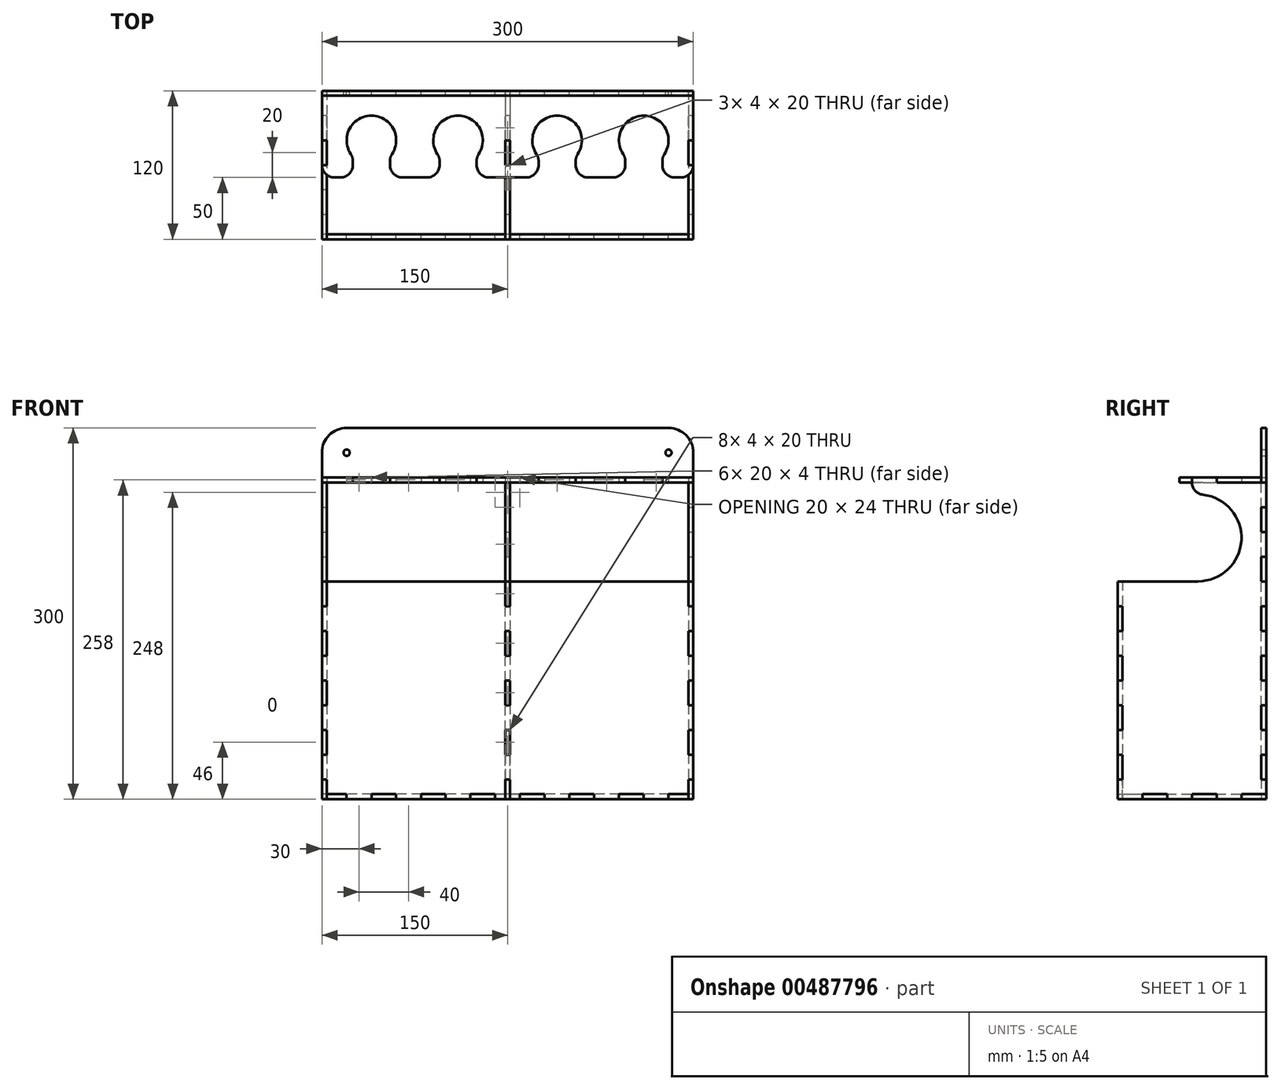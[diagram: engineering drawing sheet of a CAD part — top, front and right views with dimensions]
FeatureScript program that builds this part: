
annotation { "Feature Type Name" : "Feature", "Feature Type Description" : "" }
export const myFeature = defineFeature(function(context is Context, id is Id, definition is map)
    precondition{}
    {
        {
            var Q0;
            Q0=qCreatedBy(makeId("Front.planeOp"),FACE);
            var sketch = newSketch(context, id + "F0", { "sketchPlane" : qUnion([Q0])});
            skLineSegment(sketch, "E0.bottom", {"start": v(-130, 150) * mm, "end": v(130, 150) * mm});
            skLineSegment(sketch, "E0.top", {"start": v(-130, -150) * mm, "end": v(-110, -150) * mm});
            skLineSegment(sketch, "E0.left", {"start": v(-150, 130) * mm, "end": v(-150, 106) * mm});
            skLineSegment(sketch, "E0.right", {"start": v(150, 130) * mm, "end": v(150, 106) * mm});
            skPoint(sketch, "E0.middle", {"position": v(0, 0) * mm});
            skPoint(sketch, "E1.visualSharp", {"position": v(-150, 150) * mm});
            skArc(sketch, "E1.filletArc", {"start": v(-130, 150) * mm, "mid": v(-144.14, 144.14) * mm, "end": v(-150, 130) * mm});
            skPoint(sketch, "E2.visualSharp", {"position": v(150, 150) * mm});
            skArc(sketch, "E2.filletArc", {"start": v(150, 130) * mm, "mid": v(144.14, 144.14) * mm, "end": v(130, 150) * mm});
            skLineSegment(sketch, "E3", {"start": v(-130, 110) * mm, "end": v(-110, 110) * mm});
            skLineSegment(sketch, "E4", {"start": v(-150, 106) * mm, "end": v(-146, 106) * mm});
            skLineSegment(sketch, "E5", {"start": v(-146, 106) * mm, "end": v(-146, 86) * mm});
            skLineSegment(sketch, "E6", {"start": v(146, 106) * mm, "end": v(146, 46) * mm});
            skLineSegment(sketch, "E7", {"start": v(-146, -146) * mm, "end": v(-130, -146) * mm});
            skCircle(sketch, "E8", {"center": v(-130, 130) * mm, "radius": 2.5 * mm});
            skLineSegment(sketch, "E9", {"start": v(-130, 110) * mm, "end": v(-130, 106) * mm});
            skLineSegment(sketch, "E10.1.0.0", {"start": v(-110, 110) * mm, "end": v(-110, 106) * mm});
            skLineSegment(sketch, "E10.2.0.0", {"start": v(-90, 110) * mm, "end": v(-90, 106) * mm});
            skLineSegment(sketch, "E10.3.0.0", {"start": v(-70, 110) * mm, "end": v(-70, 106) * mm});
            skLineSegment(sketch, "E10.4.0.0", {"start": v(-50, 110) * mm, "end": v(-50, 106) * mm});
            skLineSegment(sketch, "E10.5.0.0", {"start": v(-30, 110) * mm, "end": v(-30, 106) * mm});
            skLineSegment(sketch, "E10.6.0.0", {"start": v(-10, 110) * mm, "end": v(-10, 106) * mm});
            skLineSegment(sketch, "E10.7.0.0", {"start": v(10, 110) * mm, "end": v(10, 106) * mm});
            skLineSegment(sketch, "E10.8.0.0", {"start": v(30, 110) * mm, "end": v(30, 106) * mm});
            skLineSegment(sketch, "E10.9.0.0", {"start": v(50, 110) * mm, "end": v(50, 106) * mm});
            skLineSegment(sketch, "E10.10.0.0", {"start": v(70, 110) * mm, "end": v(70, 106) * mm});
            skLineSegment(sketch, "E10.11.0.0", {"start": v(90, 110) * mm, "end": v(90, 106) * mm});
            skLineSegment(sketch, "E10.12.0.0", {"start": v(110, 110) * mm, "end": v(110, 106) * mm});
            skLineSegment(sketch, "E10.13.0.0", {"start": v(130, 110) * mm, "end": v(130, 106) * mm});
            skLineSegment(sketch, "E10.direction1", {"start": v(-130, 106) * mm, "end": v(-110, 106) * mm, "construction": true});
            skLineSegment(sketch, "E11.trimOffspring", {"start": v(-130, 106) * mm, "end": v(-110, 106) * mm});
            skLineSegment(sketch, "E12.trimOffspring", {"start": v(-90, 110) * mm, "end": v(-70, 110) * mm});
            skLineSegment(sketch, "E13.trimOffspring", {"start": v(-90, 106) * mm, "end": v(-70, 106) * mm});
            skLineSegment(sketch, "E14.trimOffspring", {"start": v(-50, 110) * mm, "end": v(-30, 110) * mm});
            skLineSegment(sketch, "E15.trimOffspring", {"start": v(-50, 106) * mm, "end": v(-30, 106) * mm});
            skLineSegment(sketch, "E16.trimOffspring", {"start": v(-10, 110) * mm, "end": v(10, 110) * mm});
            skLineSegment(sketch, "E17.trimOffspring", {"start": v(-10, 106) * mm, "end": v(-2, 106) * mm});
            skLineSegment(sketch, "E18.trimOffspring", {"start": v(30, 110) * mm, "end": v(50, 110) * mm});
            skLineSegment(sketch, "E19.trimOffspring", {"start": v(30, 106) * mm, "end": v(50, 106) * mm});
            skLineSegment(sketch, "E20.trimOffspring", {"start": v(70, 110) * mm, "end": v(90, 110) * mm});
            skLineSegment(sketch, "E21.trimOffspring", {"start": v(70, 106) * mm, "end": v(90, 106) * mm});
            skLineSegment(sketch, "E22.trimOffspring", {"start": v(110, 110) * mm, "end": v(130, 110) * mm});
            skLineSegment(sketch, "E23.trimOffspring", {"start": v(110, 106) * mm, "end": v(130, 106) * mm});
            skLineSegment(sketch, "E24.trimOffspring", {"start": v(146, 106) * mm, "end": v(150, 106) * mm});
            skLineSegment(sketch, "E25", {"start": v(-150, 86) * mm, "end": v(-146, 86) * mm});
            skLineSegment(sketch, "E26.0.1.0", {"start": v(-150, 66) * mm, "end": v(-146, 66) * mm});
            skLineSegment(sketch, "E26.0.2.0", {"start": v(-150, 46) * mm, "end": v(-146, 46) * mm});
            skLineSegment(sketch, "E26.0.3.0", {"start": v(-150, 26) * mm, "end": v(-146, 26) * mm});
            skLineSegment(sketch, "E26.0.4.0", {"start": v(-150, 6) * mm, "end": v(-146, 6) * mm});
            skLineSegment(sketch, "E26.0.5.0", {"start": v(-150, -14) * mm, "end": v(-146, -14) * mm});
            skLineSegment(sketch, "E26.0.6.0", {"start": v(-150, -34) * mm, "end": v(-146, -34) * mm});
            skLineSegment(sketch, "E26.0.7.0", {"start": v(-150, -54) * mm, "end": v(-146, -54) * mm});
            skLineSegment(sketch, "E26.0.8.0", {"start": v(-150, -74) * mm, "end": v(-146, -74) * mm});
            skLineSegment(sketch, "E26.0.9.0", {"start": v(-150, -94) * mm, "end": v(-146, -94) * mm});
            skLineSegment(sketch, "E26.0.10.0", {"start": v(-150, -114) * mm, "end": v(-146, -114) * mm});
            skLineSegment(sketch, "E26.0.11.0", {"start": v(-150, -134) * mm, "end": v(-146, -134) * mm});
            skLineSegment(sketch, "E26.direction1", {"start": v(-150, 86) * mm, "end": v(-125, 86) * mm, "construction": true});
            skLineSegment(sketch, "E26.direction2", {"start": v(-150, 86) * mm, "end": v(-150, 66) * mm, "construction": true});
            skLineSegment(sketch, "E27.trimOffspring", {"start": v(-150, 86) * mm, "end": v(-150, 66) * mm});
            skLineSegment(sketch, "E28.trimOffspring", {"start": v(-146, 66) * mm, "end": v(-146, 46) * mm});
            skLineSegment(sketch, "E29.trimOffspring", {"start": v(-150, 46) * mm, "end": v(-150, 26) * mm});
            skLineSegment(sketch, "E30.trimOffspring", {"start": v(-146, 26) * mm, "end": v(-146, 6) * mm});
            skLineSegment(sketch, "E31.trimOffspring", {"start": v(-150, 6) * mm, "end": v(-150, -14) * mm});
            skLineSegment(sketch, "E32.trimOffspring", {"start": v(-146, -14) * mm, "end": v(-146, -34) * mm});
            skLineSegment(sketch, "E33.trimOffspring", {"start": v(-150, -34) * mm, "end": v(-150, -54) * mm});
            skLineSegment(sketch, "E34.trimOffspring", {"start": v(-146, -54) * mm, "end": v(-146, -74) * mm});
            skLineSegment(sketch, "E35.trimOffspring", {"start": v(-150, -74) * mm, "end": v(-150, -94) * mm});
            skLineSegment(sketch, "E36.trimOffspring", {"start": v(-150, -114) * mm, "end": v(-150, -134) * mm});
            skLineSegment(sketch, "E37.trimOffspring", {"start": v(-146, -134) * mm, "end": v(-146, -146) * mm});
            skLineSegment(sketch, "E38", {"start": v(-130, -146) * mm, "end": v(-130, -150) * mm});
            skLineSegment(sketch, "E39.1.0.0", {"start": v(-110, -146) * mm, "end": v(-110, -150) * mm});
            skLineSegment(sketch, "E39.2.0.0", {"start": v(-90, -146) * mm, "end": v(-90, -150) * mm});
            skLineSegment(sketch, "E39.3.0.0", {"start": v(-70, -146) * mm, "end": v(-70, -150) * mm});
            skLineSegment(sketch, "E39.4.0.0", {"start": v(-50, -146) * mm, "end": v(-50, -150) * mm});
            skLineSegment(sketch, "E39.5.0.0", {"start": v(-30, -146) * mm, "end": v(-30, -150) * mm});
            skLineSegment(sketch, "E39.6.0.0", {"start": v(-10, -146) * mm, "end": v(-10, -150) * mm});
            skLineSegment(sketch, "E39.7.0.0", {"start": v(10, -146) * mm, "end": v(10, -150) * mm});
            skLineSegment(sketch, "E39.8.0.0", {"start": v(30, -146) * mm, "end": v(30, -150) * mm});
            skLineSegment(sketch, "E39.9.0.0", {"start": v(50, -146) * mm, "end": v(50, -150) * mm});
            skLineSegment(sketch, "E39.10.0.0", {"start": v(70, -146) * mm, "end": v(70, -150) * mm});
            skLineSegment(sketch, "E39.11.0.0", {"start": v(90, -146) * mm, "end": v(90, -150) * mm});
            skLineSegment(sketch, "E39.12.0.0", {"start": v(110, -146) * mm, "end": v(110, -150) * mm});
            skLineSegment(sketch, "E39.13.0.0", {"start": v(130, -146) * mm, "end": v(130, -150) * mm});
            skLineSegment(sketch, "E39.direction1", {"start": v(-130, -150) * mm, "end": v(-110, -150) * mm, "construction": true});
            skLineSegment(sketch, "E40.trimOffspring", {"start": v(-110, -146) * mm, "end": v(-90, -146) * mm});
            skLineSegment(sketch, "E41.trimOffspring", {"start": v(-90, -150) * mm, "end": v(-70, -150) * mm});
            skLineSegment(sketch, "E42.trimOffspring", {"start": v(-70, -146) * mm, "end": v(-50, -146) * mm});
            skLineSegment(sketch, "E43.trimOffspring", {"start": v(-50, -150) * mm, "end": v(-30, -150) * mm});
            skLineSegment(sketch, "E44.trimOffspring", {"start": v(-30, -146) * mm, "end": v(-10, -146) * mm});
            skLineSegment(sketch, "E45.trimOffspring", {"start": v(-10, -150) * mm, "end": v(10, -150) * mm});
            skLineSegment(sketch, "E46.trimOffspring", {"start": v(10, -146) * mm, "end": v(30, -146) * mm});
            skLineSegment(sketch, "E47.trimOffspring", {"start": v(30, -150) * mm, "end": v(50, -150) * mm});
            skLineSegment(sketch, "E48.trimOffspring", {"start": v(50, -146) * mm, "end": v(70, -146) * mm});
            skLineSegment(sketch, "E49.trimOffspring", {"start": v(70, -150) * mm, "end": v(90, -150) * mm});
            skLineSegment(sketch, "E50.trimOffspring", {"start": v(90, -146) * mm, "end": v(110, -146) * mm});
            skLineSegment(sketch, "E51.trimOffspring", {"start": v(110, -150) * mm, "end": v(130, -150) * mm});
            skLineSegment(sketch, "E52.trimOffspring", {"start": v(130, -146) * mm, "end": v(146, -146) * mm});
            skLineSegment(sketch, "E53.trimOffspring", {"start": v(-146, -94) * mm, "end": v(-146, -114) * mm});
            skCircle(sketch, "E54.MirrorC", {"center": v(130, 130) * mm, "radius": 2.5 * mm});
            skLineSegment(sketch, "E55", {"start": v(146, 86) * mm, "end": v(150, 86) * mm});
            skLineSegment(sketch, "E56.0.1.0", {"start": v(146, 66) * mm, "end": v(150, 66) * mm});
            skLineSegment(sketch, "E56.0.2.0", {"start": v(146, 46) * mm, "end": v(150, 46) * mm});
            skLineSegment(sketch, "E56.0.3.0", {"start": v(146, 26) * mm, "end": v(150, 26) * mm});
            skLineSegment(sketch, "E56.0.4.0", {"start": v(146, 6) * mm, "end": v(150, 6) * mm});
            skLineSegment(sketch, "E56.0.5.0", {"start": v(146, -14) * mm, "end": v(150, -14) * mm});
            skLineSegment(sketch, "E56.0.6.0", {"start": v(146, -34) * mm, "end": v(150, -34) * mm});
            skLineSegment(sketch, "E56.0.7.0", {"start": v(146, -54) * mm, "end": v(150, -54) * mm});
            skLineSegment(sketch, "E56.0.8.0", {"start": v(146, -74) * mm, "end": v(150, -74) * mm});
            skLineSegment(sketch, "E56.0.9.0", {"start": v(146, -94) * mm, "end": v(150, -94) * mm});
            skLineSegment(sketch, "E56.0.10.0", {"start": v(146, -114) * mm, "end": v(150, -114) * mm});
            skLineSegment(sketch, "E56.0.11.0", {"start": v(146, -134) * mm, "end": v(150, -134) * mm});
            skLineSegment(sketch, "E56.direction1", {"start": v(146, 86) * mm, "end": v(171, 86) * mm, "construction": true});
            skLineSegment(sketch, "E57.trimOffspring", {"start": v(146, -134) * mm, "end": v(146, -146) * mm});
            skLineSegment(sketch, "E58.trimOffspring", {"start": v(150, -114) * mm, "end": v(150, -134) * mm});
            skLineSegment(sketch, "E59.trimOffspring", {"start": v(146, -94) * mm, "end": v(146, -114) * mm});
            skLineSegment(sketch, "E60.trimOffspring", {"start": v(150, -74) * mm, "end": v(150, -94) * mm});
            skLineSegment(sketch, "E61.trimOffspring", {"start": v(146, -54) * mm, "end": v(146, -74) * mm});
            skLineSegment(sketch, "E62.trimOffspring", {"start": v(150, -34) * mm, "end": v(150, -54) * mm});
            skLineSegment(sketch, "E63.trimOffspring", {"start": v(146, -14) * mm, "end": v(146, -34) * mm});
            skLineSegment(sketch, "E64.trimOffspring", {"start": v(150, 6) * mm, "end": v(150, -14) * mm});
            skLineSegment(sketch, "E65.trimOffspring", {"start": v(146, 26) * mm, "end": v(146, 6) * mm});
            skLineSegment(sketch, "E66.trimOffspring", {"start": v(150, 46) * mm, "end": v(150, 26) * mm});
            skLineSegment(sketch, "E67.trimOffspring", {"start": v(150, 86) * mm, "end": v(150, 66) * mm});
            skLineSegment(sketch, "E68.bottom", {"start": v(-2, 86) * mm, "end": v(2, 86) * mm});
            skLineSegment(sketch, "E68.left", {"start": v(-2, 86) * mm, "end": v(-2, 106) * mm});
            skLineSegment(sketch, "E68.right", {"start": v(2, 86) * mm, "end": v(2, 106) * mm});
            skPoint(sketch, "E68.middle", {"position": v(0, 96) * mm});
            skLineSegment(sketch, "E69.0.1.0", {"start": v(-2, 46) * mm, "end": v(-2, 66) * mm});
            skLineSegment(sketch, "E69.0.1.1", {"start": v(2, 46) * mm, "end": v(2, 66) * mm});
            skLineSegment(sketch, "E69.0.1.2", {"start": v(-2, 46) * mm, "end": v(2, 46) * mm});
            skLineSegment(sketch, "E69.0.1.3", {"start": v(-2, 66) * mm, "end": v(2, 66) * mm});
            skPoint(sketch, "E69.0.1.4", {"position": v(0, 56) * mm});
            skLineSegment(sketch, "E69.0.2.0", {"start": v(-2, 6) * mm, "end": v(-2, 26) * mm});
            skLineSegment(sketch, "E69.0.2.1", {"start": v(2, 6) * mm, "end": v(2, 26) * mm});
            skLineSegment(sketch, "E69.0.2.2", {"start": v(-2, 6) * mm, "end": v(2, 6) * mm});
            skLineSegment(sketch, "E69.0.2.3", {"start": v(-2, 26) * mm, "end": v(2, 26) * mm});
            skPoint(sketch, "E69.0.2.4", {"position": v(0, 16) * mm});
            skLineSegment(sketch, "E69.0.3.0", {"start": v(-2, -34) * mm, "end": v(-2, -14) * mm});
            skLineSegment(sketch, "E69.0.3.1", {"start": v(2, -34) * mm, "end": v(2, -14) * mm});
            skLineSegment(sketch, "E69.0.3.2", {"start": v(-2, -34) * mm, "end": v(2, -34) * mm});
            skLineSegment(sketch, "E69.0.3.3", {"start": v(-2, -14) * mm, "end": v(2, -14) * mm});
            skPoint(sketch, "E69.0.3.4", {"position": v(0, -24) * mm});
            skLineSegment(sketch, "E69.0.4.0", {"start": v(-2, -74) * mm, "end": v(-2, -54) * mm});
            skLineSegment(sketch, "E69.0.4.1", {"start": v(2, -74) * mm, "end": v(2, -54) * mm});
            skLineSegment(sketch, "E69.0.4.2", {"start": v(-2, -74) * mm, "end": v(2, -74) * mm});
            skLineSegment(sketch, "E69.0.4.3", {"start": v(-2, -54) * mm, "end": v(2, -54) * mm});
            skPoint(sketch, "E69.0.4.4", {"position": v(0, -64) * mm});
            skLineSegment(sketch, "E69.0.5.0", {"start": v(-2, -114) * mm, "end": v(-2, -94) * mm});
            skLineSegment(sketch, "E69.0.5.1", {"start": v(2, -114) * mm, "end": v(2, -94) * mm});
            skLineSegment(sketch, "E69.0.5.2", {"start": v(-2, -114) * mm, "end": v(2, -114) * mm});
            skLineSegment(sketch, "E69.0.5.3", {"start": v(-2, -94) * mm, "end": v(2, -94) * mm});
            skPoint(sketch, "E69.0.5.4", {"position": v(0, -104) * mm});
            skLineSegment(sketch, "E69.direction1", {"start": v(-2, 86) * mm, "end": v(23, 86) * mm, "construction": true});
            skLineSegment(sketch, "E69.direction2", {"start": v(-2, 86) * mm, "end": v(-2, 46) * mm, "construction": true});
            skLineSegment(sketch, "E70.trimOffspring", {"start": v(2, 106) * mm, "end": v(10, 106) * mm});
            skSolve(sketch);
        }
        {
            var Q0;
            Q0 = qSketchRegion(id + "F0", true);
            extrude(context, id + "F1", {"entities" : qUnion([Q0]), "depth" : 4 * mm});
        }
        {
            var Q0;
            Q0=makeQuery(id+"F1.opExtrude","SWEPT_FACE",FACE,{"disambiguationData":[OSD([sQuery(id+"F0.wireOp",EDGE,"E11.trimOffspring")])]});
            var sketch = newSketch(context, id + "F2", { "sketchPlane" : qUnion([Q0])});
            skLineSegment(sketch, "E71.bottom", {"start": v(-150, 0) * mm, "end": v(150, 0) * mm});
            skLineSegment(sketch, "E71.top", {"start": v(-140, -70) * mm, "end": v(-135, -70) * mm});
            skLineSegment(sketch, "E71.left", {"start": v(-150, 0) * mm, "end": v(-150, -40) * mm});
            skLineSegment(sketch, "E71.right", {"start": v(150, 0) * mm, "end": v(150, -40) * mm});
            skPoint(sketch, "E72.visualSharp", {"position": v(-150, -70) * mm});
            skArc(sketch, "E72.filletArc", {"start": v(-150, -60) * mm, "mid": v(-147.07, -67.07) * mm, "end": v(-140, -70) * mm});
            skPoint(sketch, "E73.visualSharp", {"position": v(150, -70) * mm});
            skArc(sketch, "E73.filletArc", {"start": v(140, -70) * mm, "mid": v(147.07, -67.07) * mm, "end": v(150, -60) * mm});
            skArc(sketch, "E74", {"start": v(-93.33, -51.06) * mm, "mid": v(-110, -20) * mm, "end": v(-126.67, -51.06) * mm});
            skArc(sketch, "E75", {"start": v(-23.33, -51.06) * mm, "mid": v(-40, -20) * mm, "end": v(-56.67, -51.06) * mm});
            skArc(sketch, "E76", {"start": v(56.67, -51.06) * mm, "mid": v(40, -20) * mm, "end": v(23.33, -51.06) * mm});
            skArc(sketch, "E77", {"start": v(126.67, -51.06) * mm, "mid": v(110, -20) * mm, "end": v(93.33, -51.06) * mm});
            skLineSegment(sketch, "E78", {"start": v(-110, -40) * mm, "end": v(-40, -40) * mm, "construction": true});
            skLineSegment(sketch, "E79", {"start": v(40, -40) * mm, "end": v(110, -40) * mm, "construction": true});
            skLineSegment(sketch, "E80", {"start": v(-125, -60) * mm, "end": v(-125, -56.58) * mm});
            skLineSegment(sketch, "E81", {"start": v(-95, -60) * mm, "end": v(-95, -56.58) * mm});
            skLineSegment(sketch, "E82.trimOffspring", {"start": v(-85, -70) * mm, "end": v(-65, -70) * mm});
            skPoint(sketch, "E83.visualSharp", {"position": v(-125, -53.23) * mm});
            skArc(sketch, "E83.filletArc", {"start": v(-125, -56.58) * mm, "mid": v(-125.43, -53.7) * mm, "end": v(-126.67, -51.06) * mm});
            skPoint(sketch, "E84.visualSharp", {"position": v(-125, -70) * mm});
            skArc(sketch, "E84.filletArc", {"start": v(-135, -70) * mm, "mid": v(-127.93, -67.07) * mm, "end": v(-125, -60) * mm});
            skPoint(sketch, "E85.visualSharp", {"position": v(-95, -53.23) * mm});
            skArc(sketch, "E85.filletArc", {"start": v(-93.33, -51.06) * mm, "mid": v(-94.57, -53.7) * mm, "end": v(-95, -56.58) * mm});
            skPoint(sketch, "E86.visualSharp", {"position": v(-95, -70) * mm});
            skArc(sketch, "E86.filletArc", {"start": v(-95, -60) * mm, "mid": v(-92.07, -67.07) * mm, "end": v(-85, -70) * mm});
            skLineSegment(sketch, "E87", {"start": v(-55, -56.58) * mm, "end": v(-55, -60) * mm});
            skLineSegment(sketch, "E88", {"start": v(-25, -56.58) * mm, "end": v(-25, -60) * mm});
            skLineSegment(sketch, "E89.trimOffspring", {"start": v(-15, -70) * mm, "end": v(15, -70) * mm});
            skLineSegment(sketch, "E90", {"start": v(25, -56.58) * mm, "end": v(25, -60) * mm});
            skLineSegment(sketch, "E91", {"start": v(55, -56.58) * mm, "end": v(55, -60) * mm});
            skLineSegment(sketch, "E92", {"start": v(95, -56.58) * mm, "end": v(95, -60) * mm});
            skLineSegment(sketch, "E93", {"start": v(125, -56.58) * mm, "end": v(125, -60) * mm});
            skLineSegment(sketch, "E94.trimOffspring", {"start": v(65, -70) * mm, "end": v(85, -70) * mm});
            skLineSegment(sketch, "E95.trimOffspring", {"start": v(135, -70) * mm, "end": v(140, -70) * mm});
            skPoint(sketch, "E96.visualSharp", {"position": v(-55, -53.23) * mm});
            skArc(sketch, "E96.filletArc", {"start": v(-55, -56.58) * mm, "mid": v(-55.43, -53.7) * mm, "end": v(-56.67, -51.06) * mm});
            skPoint(sketch, "E97.visualSharp", {"position": v(-55, -70) * mm});
            skArc(sketch, "E97.filletArc", {"start": v(-65, -70) * mm, "mid": v(-57.93, -67.07) * mm, "end": v(-55, -60) * mm});
            skPoint(sketch, "E98.visualSharp", {"position": v(-25, -53.23) * mm});
            skArc(sketch, "E98.filletArc", {"start": v(-23.33, -51.06) * mm, "mid": v(-24.57, -53.7) * mm, "end": v(-25, -56.58) * mm});
            skPoint(sketch, "E99.visualSharp", {"position": v(-25, -70) * mm});
            skArc(sketch, "E99.filletArc", {"start": v(-25, -60) * mm, "mid": v(-22.07, -67.07) * mm, "end": v(-15, -70) * mm});
            skPoint(sketch, "E100.visualSharp", {"position": v(25, -53.23) * mm});
            skArc(sketch, "E100.filletArc", {"start": v(25, -56.58) * mm, "mid": v(24.57, -53.7) * mm, "end": v(23.33, -51.06) * mm});
            skPoint(sketch, "E101.visualSharp", {"position": v(25, -70) * mm});
            skArc(sketch, "E101.filletArc", {"start": v(15, -70) * mm, "mid": v(22.07, -67.07) * mm, "end": v(25, -60) * mm});
            skPoint(sketch, "E102.visualSharp", {"position": v(55, -53.23) * mm});
            skArc(sketch, "E102.filletArc", {"start": v(56.67, -51.06) * mm, "mid": v(55.43, -53.7) * mm, "end": v(55, -56.58) * mm});
            skPoint(sketch, "E103.visualSharp", {"position": v(55, -70) * mm});
            skArc(sketch, "E103.filletArc", {"start": v(55, -60) * mm, "mid": v(57.93, -67.07) * mm, "end": v(65, -70) * mm});
            skPoint(sketch, "E104.visualSharp", {"position": v(95, -70) * mm});
            skArc(sketch, "E104.filletArc", {"start": v(85, -70) * mm, "mid": v(92.07, -67.07) * mm, "end": v(95, -60) * mm});
            skPoint(sketch, "E105.visualSharp", {"position": v(95, -53.23) * mm});
            skArc(sketch, "E105.filletArc", {"start": v(95, -56.58) * mm, "mid": v(94.57, -53.7) * mm, "end": v(93.33, -51.06) * mm});
            skPoint(sketch, "E106.visualSharp", {"position": v(125, -53.23) * mm});
            skArc(sketch, "E106.filletArc", {"start": v(126.67, -51.06) * mm, "mid": v(125.43, -53.7) * mm, "end": v(125, -56.58) * mm});
            skPoint(sketch, "E107.visualSharp", {"position": v(125, -70) * mm});
            skArc(sketch, "E107.filletArc", {"start": v(125, -60) * mm, "mid": v(127.93, -67.07) * mm, "end": v(135, -70) * mm});
            skLineSegment(sketch, "E108.bottom", {"start": v(-2, -60) * mm, "end": v(2, -60) * mm});
            skLineSegment(sketch, "E108.top", {"start": v(-2, -40) * mm, "end": v(2, -40) * mm});
            skLineSegment(sketch, "E108.left", {"start": v(-2, -60) * mm, "end": v(-2, -40) * mm});
            skLineSegment(sketch, "E108.right", {"start": v(2, -60) * mm, "end": v(2, -40) * mm});
            skPoint(sketch, "E108.middle", {"position": v(0, -50) * mm});
            skLineSegment(sketch, "E109", {"start": v(-150, -60) * mm, "end": v(-146, -60) * mm});
            skLineSegment(sketch, "E110", {"start": v(-146, -60) * mm, "end": v(-146, -40) * mm});
            skLineSegment(sketch, "E111", {"start": v(-146, -40) * mm, "end": v(-150, -40) * mm});
            skLineSegment(sketch, "E112", {"start": v(150, -60) * mm, "end": v(146, -60) * mm});
            skLineSegment(sketch, "E113", {"start": v(146, -60) * mm, "end": v(146, -40) * mm});
            skLineSegment(sketch, "E114", {"start": v(146, -40) * mm, "end": v(150, -40) * mm});
            skSolve(sketch);
        }
        {
            var Q0;
            Q0 = qSketchRegion(id + "F2", true);
            extrude(context, id + "F3", {"entities" : qUnion([Q0]), "depth" : 4 * mm});
        }
        {
            var Q0;
            Q0=makeQuery(id+"F1.opExtrude","SWEPT_BODY",BODY,{"disambiguationData":[OSD([sQuery(id+"F0.wireOp",EDGE,"E0.bottom"),sQuery(id+"F0.wireOp",EDGE,"E0.top"),sQuery(id+"F0.wireOp",EDGE,"E0.left"),sQuery(id+"F0.wireOp",EDGE,"E0.right"),sQuery(id+"F0.wireOp",EDGE,"E1.filletArc"),sQuery(id+"F0.wireOp",EDGE,"E2.filletArc"),sQuery(id+"F0.wireOp",EDGE,"E3"),sQuery(id+"F0.wireOp",EDGE,"E4"),sQuery(id+"F0.wireOp",EDGE,"E5"),sQuery(id+"F0.wireOp",EDGE,"E6"),sQuery(id+"F0.wireOp",EDGE,"E7"),sQuery(id+"F0.wireOp",EDGE,"E8"),sQuery(id+"F0.wireOp",EDGE,"E9"),sQuery(id+"F0.wireOp",EDGE,"E10.1.0.0"),sQuery(id+"F0.wireOp",EDGE,"E10.2.0.0"),sQuery(id+"F0.wireOp",EDGE,"E10.3.0.0"),sQuery(id+"F0.wireOp",EDGE,"E10.4.0.0"),sQuery(id+"F0.wireOp",EDGE,"E10.5.0.0"),sQuery(id+"F0.wireOp",EDGE,"E10.6.0.0"),sQuery(id+"F0.wireOp",EDGE,"E10.7.0.0"),sQuery(id+"F0.wireOp",EDGE,"E10.8.0.0"),sQuery(id+"F0.wireOp",EDGE,"E10.9.0.0"),sQuery(id+"F0.wireOp",EDGE,"E10.10.0.0"),sQuery(id+"F0.wireOp",EDGE,"E10.11.0.0"),sQuery(id+"F0.wireOp",EDGE,"E10.12.0.0"),sQuery(id+"F0.wireOp",EDGE,"E10.13.0.0"),sQuery(id+"F0.wireOp",EDGE,"E11.trimOffspring"),sQuery(id+"F0.wireOp",EDGE,"E12.trimOffspring"),sQuery(id+"F0.wireOp",EDGE,"E13.trimOffspring"),sQuery(id+"F0.wireOp",EDGE,"E14.trimOffspring"),sQuery(id+"F0.wireOp",EDGE,"E15.trimOffspring"),sQuery(id+"F0.wireOp",EDGE,"E16.trimOffspring"),sQuery(id+"F0.wireOp",EDGE,"E17.trimOffspring"),sQuery(id+"F0.wireOp",EDGE,"E18.trimOffspring"),sQuery(id+"F0.wireOp",EDGE,"E19.trimOffspring"),sQuery(id+"F0.wireOp",EDGE,"E20.trimOffspring"),sQuery(id+"F0.wireOp",EDGE,"E21.trimOffspring"),sQuery(id+"F0.wireOp",EDGE,"E22.trimOffspring"),sQuery(id+"F0.wireOp",EDGE,"E23.trimOffspring"),sQuery(id+"F0.wireOp",EDGE,"E24.trimOffspring"),sQuery(id+"F0.wireOp",EDGE,"E25"),sQuery(id+"F0.wireOp",EDGE,"E26.0.1.0"),sQuery(id+"F0.wireOp",EDGE,"E26.0.2.0"),sQuery(id+"F0.wireOp",EDGE,"E26.0.3.0"),sQuery(id+"F0.wireOp",EDGE,"E26.0.4.0"),sQuery(id+"F0.wireOp",EDGE,"E26.0.5.0"),sQuery(id+"F0.wireOp",EDGE,"E26.0.6.0"),sQuery(id+"F0.wireOp",EDGE,"E26.0.7.0"),sQuery(id+"F0.wireOp",EDGE,"E26.0.8.0"),sQuery(id+"F0.wireOp",EDGE,"E26.0.9.0"),sQuery(id+"F0.wireOp",EDGE,"E26.0.10.0"),sQuery(id+"F0.wireOp",EDGE,"E26.0.11.0"),sQuery(id+"F0.wireOp",EDGE,"E27.trimOffspring"),sQuery(id+"F0.wireOp",EDGE,"E28.trimOffspring"),sQuery(id+"F0.wireOp",EDGE,"E29.trimOffspring"),sQuery(id+"F0.wireOp",EDGE,"E30.trimOffspring"),sQuery(id+"F0.wireOp",EDGE,"E31.trimOffspring"),sQuery(id+"F0.wireOp",EDGE,"E32.trimOffspring"),sQuery(id+"F0.wireOp",EDGE,"E33.trimOffspring"),sQuery(id+"F0.wireOp",EDGE,"E34.trimOffspring"),sQuery(id+"F0.wireOp",EDGE,"E35.trimOffspring"),sQuery(id+"F0.wireOp",EDGE,"E36.trimOffspring"),sQuery(id+"F0.wireOp",EDGE,"E37.trimOffspring"),sQuery(id+"F0.wireOp",EDGE,"E38"),sQuery(id+"F0.wireOp",EDGE,"E39.1.0.0"),sQuery(id+"F0.wireOp",EDGE,"E39.2.0.0"),sQuery(id+"F0.wireOp",EDGE,"E39.3.0.0"),sQuery(id+"F0.wireOp",EDGE,"E39.4.0.0"),sQuery(id+"F0.wireOp",EDGE,"E39.5.0.0"),sQuery(id+"F0.wireOp",EDGE,"E39.6.0.0"),sQuery(id+"F0.wireOp",EDGE,"E39.7.0.0"),sQuery(id+"F0.wireOp",EDGE,"E39.8.0.0"),sQuery(id+"F0.wireOp",EDGE,"E39.9.0.0"),sQuery(id+"F0.wireOp",EDGE,"E39.10.0.0"),sQuery(id+"F0.wireOp",EDGE,"E39.11.0.0"),sQuery(id+"F0.wireOp",EDGE,"E39.12.0.0"),sQuery(id+"F0.wireOp",EDGE,"E39.13.0.0"),sQuery(id+"F0.wireOp",EDGE,"E40.trimOffspring"),sQuery(id+"F0.wireOp",EDGE,"E41.trimOffspring"),sQuery(id+"F0.wireOp",EDGE,"E42.trimOffspring"),sQuery(id+"F0.wireOp",EDGE,"E43.trimOffspring"),sQuery(id+"F0.wireOp",EDGE,"E44.trimOffspring"),sQuery(id+"F0.wireOp",EDGE,"E45.trimOffspring"),sQuery(id+"F0.wireOp",EDGE,"E46.trimOffspring"),sQuery(id+"F0.wireOp",EDGE,"E47.trimOffspring"),sQuery(id+"F0.wireOp",EDGE,"E48.trimOffspring"),sQuery(id+"F0.wireOp",EDGE,"E49.trimOffspring"),sQuery(id+"F0.wireOp",EDGE,"E50.trimOffspring"),sQuery(id+"F0.wireOp",EDGE,"E51.trimOffspring"),sQuery(id+"F0.wireOp",EDGE,"E52.trimOffspring"),sQuery(id+"F0.wireOp",EDGE,"E53.trimOffspring"),sQuery(id+"F0.wireOp",EDGE,"E54.MirrorC"),sQuery(id+"F0.wireOp",EDGE,"E55"),sQuery(id+"F0.wireOp",EDGE,"E56.0.1.0"),sQuery(id+"F0.wireOp",EDGE,"E56.0.2.0"),sQuery(id+"F0.wireOp",EDGE,"E56.0.3.0"),sQuery(id+"F0.wireOp",EDGE,"E56.0.4.0"),sQuery(id+"F0.wireOp",EDGE,"E56.0.5.0"),sQuery(id+"F0.wireOp",EDGE,"E56.0.6.0"),sQuery(id+"F0.wireOp",EDGE,"E56.0.7.0"),sQuery(id+"F0.wireOp",EDGE,"E56.0.8.0"),sQuery(id+"F0.wireOp",EDGE,"E56.0.9.0"),sQuery(id+"F0.wireOp",EDGE,"E56.0.10.0"),sQuery(id+"F0.wireOp",EDGE,"E56.0.11.0"),sQuery(id+"F0.wireOp",EDGE,"E57.trimOffspring"),sQuery(id+"F0.wireOp",EDGE,"E58.trimOffspring"),sQuery(id+"F0.wireOp",EDGE,"E59.trimOffspring"),sQuery(id+"F0.wireOp",EDGE,"E60.trimOffspring"),sQuery(id+"F0.wireOp",EDGE,"E61.trimOffspring"),sQuery(id+"F0.wireOp",EDGE,"E62.trimOffspring"),sQuery(id+"F0.wireOp",EDGE,"E63.trimOffspring"),sQuery(id+"F0.wireOp",EDGE,"E64.trimOffspring"),sQuery(id+"F0.wireOp",EDGE,"E65.trimOffspring"),sQuery(id+"F0.wireOp",EDGE,"E66.trimOffspring"),sQuery(id+"F0.wireOp",EDGE,"E67.trimOffspring"),sQuery(id+"F0.wireOp",EDGE,"E68.bottom"),sQuery(id+"F0.wireOp",EDGE,"E68.left"),sQuery(id+"F0.wireOp",EDGE,"E68.right"),sQuery(id+"F0.wireOp",EDGE,"E69.0.1.0"),sQuery(id+"F0.wireOp",EDGE,"E69.0.1.1"),sQuery(id+"F0.wireOp",EDGE,"E69.0.1.2"),sQuery(id+"F0.wireOp",EDGE,"E69.0.1.3"),sQuery(id+"F0.wireOp",EDGE,"E69.0.2.0"),sQuery(id+"F0.wireOp",EDGE,"E69.0.2.1"),sQuery(id+"F0.wireOp",EDGE,"E69.0.2.2"),sQuery(id+"F0.wireOp",EDGE,"E69.0.2.3"),sQuery(id+"F0.wireOp",EDGE,"E69.0.3.0"),sQuery(id+"F0.wireOp",EDGE,"E69.0.3.1"),sQuery(id+"F0.wireOp",EDGE,"E69.0.3.2"),sQuery(id+"F0.wireOp",EDGE,"E69.0.3.3"),sQuery(id+"F0.wireOp",EDGE,"E69.0.4.0"),sQuery(id+"F0.wireOp",EDGE,"E69.0.4.1"),sQuery(id+"F0.wireOp",EDGE,"E69.0.4.2"),sQuery(id+"F0.wireOp",EDGE,"E69.0.4.3"),sQuery(id+"F0.wireOp",EDGE,"E69.0.5.0"),sQuery(id+"F0.wireOp",EDGE,"E69.0.5.1"),sQuery(id+"F0.wireOp",EDGE,"E69.0.5.2"),sQuery(id+"F0.wireOp",EDGE,"E69.0.5.3"),sQuery(id+"F0.wireOp",EDGE,"E70.trimOffspring")])]});
            var Q1;
            Q1=makeQuery(id+"F3.opExtrude","SWEPT_BODY",BODY,{"disambiguationData":[OSD([sQuery(id+"F2.wireOp",EDGE,"E71.bottom"),sQuery(id+"F2.wireOp",EDGE,"E71.top"),sQuery(id+"F2.wireOp",EDGE,"E71.left"),sQuery(id+"F2.wireOp",EDGE,"E71.right"),sQuery(id+"F2.wireOp",EDGE,"E72.filletArc"),sQuery(id+"F2.wireOp",EDGE,"E73.filletArc"),sQuery(id+"F2.wireOp",EDGE,"E74"),sQuery(id+"F2.wireOp",EDGE,"E75"),sQuery(id+"F2.wireOp",EDGE,"E76"),sQuery(id+"F2.wireOp",EDGE,"E77"),sQuery(id+"F2.wireOp",EDGE,"E80"),sQuery(id+"F2.wireOp",EDGE,"E81"),sQuery(id+"F2.wireOp",EDGE,"E82.trimOffspring"),sQuery(id+"F2.wireOp",EDGE,"E83.filletArc"),sQuery(id+"F2.wireOp",EDGE,"E84.filletArc"),sQuery(id+"F2.wireOp",EDGE,"E85.filletArc"),sQuery(id+"F2.wireOp",EDGE,"E86.filletArc"),sQuery(id+"F2.wireOp",EDGE,"E87"),sQuery(id+"F2.wireOp",EDGE,"E88"),sQuery(id+"F2.wireOp",EDGE,"E89.trimOffspring"),sQuery(id+"F2.wireOp",EDGE,"E90"),sQuery(id+"F2.wireOp",EDGE,"E91"),sQuery(id+"F2.wireOp",EDGE,"E92"),sQuery(id+"F2.wireOp",EDGE,"E93"),sQuery(id+"F2.wireOp",EDGE,"E94.trimOffspring"),sQuery(id+"F2.wireOp",EDGE,"E95.trimOffspring"),sQuery(id+"F2.wireOp",EDGE,"E96.filletArc"),sQuery(id+"F2.wireOp",EDGE,"E97.filletArc"),sQuery(id+"F2.wireOp",EDGE,"E98.filletArc"),sQuery(id+"F2.wireOp",EDGE,"E99.filletArc"),sQuery(id+"F2.wireOp",EDGE,"E100.filletArc"),sQuery(id+"F2.wireOp",EDGE,"E101.filletArc"),sQuery(id+"F2.wireOp",EDGE,"E102.filletArc"),sQuery(id+"F2.wireOp",EDGE,"E103.filletArc"),sQuery(id+"F2.wireOp",EDGE,"E104.filletArc"),sQuery(id+"F2.wireOp",EDGE,"E105.filletArc"),sQuery(id+"F2.wireOp",EDGE,"E106.filletArc"),sQuery(id+"F2.wireOp",EDGE,"E107.filletArc"),sQuery(id+"F2.wireOp",EDGE,"E108.bottom"),sQuery(id+"F2.wireOp",EDGE,"E108.top"),sQuery(id+"F2.wireOp",EDGE,"E108.left"),sQuery(id+"F2.wireOp",EDGE,"E108.right"),sQuery(id+"F2.wireOp",EDGE,"E109"),sQuery(id+"F2.wireOp",EDGE,"E110"),sQuery(id+"F2.wireOp",EDGE,"E111"),sQuery(id+"F2.wireOp",EDGE,"E112"),sQuery(id+"F2.wireOp",EDGE,"E113"),sQuery(id+"F2.wireOp",EDGE,"E114")])]});
            booleanBodies(context, id + "F4", {"operationType" : BooleanOperationType.SUBTRACTION, "tools" : qUnion([Q0]), "targets" : qUnion([Q1]), "keepTools" : true});
        }
        {
            var Q0;
            Q0=makeQuery(id+"F3.opExtrude","SWEPT_FACE",FACE,{"disambiguationData":[OSD([sQuery(id+"F2.wireOp",EDGE,"E71.left")])]});
            var sketch = newSketch(context, id + "F5", { "sketchPlane" : qUnion([Q0])});
            skLineSegment(sketch, "E115", {"start": v(60, 110) * mm, "end": v(0, 110) * mm});
            skLineSegment(sketch, "E116", {"start": v(0, 110) * mm, "end": v(0, -146) * mm});
            skLineSegment(sketch, "E117", {"start": v(20, -150) * mm, "end": v(40, -150) * mm});
            skLineSegment(sketch, "E118", {"start": v(60, 110) * mm, "end": v(60, 106) * mm});
            skLineSegment(sketch, "E119", {"start": v(120, -150) * mm, "end": v(120, -134) * mm});
            skArc(sketch, "E120", {"start": v(51.14, 96.07) * mm, "mid": v(57.46, 99.34) * mm, "end": v(60, 106) * mm});
            skArc(sketch, "E121", {"start": v(51.14, 96.07) * mm, "mid": v(20.06, 59.14) * mm, "end": v(55.15, 26) * mm});
            skLineSegment(sketch, "E122", {"start": v(55.15, 26) * mm, "end": v(120, 26) * mm});
            skLineSegment(sketch, "E123", {"start": v(55.15, 26) * mm, "end": v(0, 26) * mm, "construction": true});
            skLineSegment(sketch, "E124", {"start": v(120, 6) * mm, "end": v(116, 6) * mm});
            skLineSegment(sketch, "E125", {"start": v(116, 6) * mm, "end": v(116, -14) * mm});
            skLineSegment(sketch, "E126", {"start": v(116, -14) * mm, "end": v(120, -14) * mm});
            skLineSegment(sketch, "E127.0.1.0", {"start": v(116, -34) * mm, "end": v(116, -54) * mm});
            skLineSegment(sketch, "E127.0.1.1", {"start": v(116, -54) * mm, "end": v(120, -54) * mm});
            skLineSegment(sketch, "E127.0.1.2", {"start": v(120, -34) * mm, "end": v(116, -34) * mm});
            skLineSegment(sketch, "E127.0.2.0", {"start": v(116, -74) * mm, "end": v(116, -94) * mm});
            skLineSegment(sketch, "E127.0.2.1", {"start": v(116, -94) * mm, "end": v(120, -94) * mm});
            skLineSegment(sketch, "E127.0.2.2", {"start": v(120, -74) * mm, "end": v(116, -74) * mm});
            skLineSegment(sketch, "E127.0.3.0", {"start": v(116, -114) * mm, "end": v(116, -134) * mm});
            skLineSegment(sketch, "E127.0.3.1", {"start": v(116, -134) * mm, "end": v(120, -134) * mm});
            skLineSegment(sketch, "E127.0.3.2", {"start": v(120, -114) * mm, "end": v(116, -114) * mm});
            skLineSegment(sketch, "E127.direction1", {"start": v(116, -14) * mm, "end": v(141, -14) * mm, "construction": true});
            skLineSegment(sketch, "E127.direction2", {"start": v(116, -14) * mm, "end": v(116, -54) * mm, "construction": true});
            skLineSegment(sketch, "E128.trimOffspring", {"start": v(120, -114) * mm, "end": v(120, -94) * mm});
            skLineSegment(sketch, "E129.trimOffspring", {"start": v(120, -74) * mm, "end": v(120, -54) * mm});
            skLineSegment(sketch, "E130.trimOffspring", {"start": v(120, -34) * mm, "end": v(120, -14) * mm});
            skLineSegment(sketch, "E131.trimOffspring", {"start": v(120, 6) * mm, "end": v(120, 26) * mm});
            skLineSegment(sketch, "E132", {"start": v(0, -146) * mm, "end": v(20, -146) * mm});
            skLineSegment(sketch, "E133", {"start": v(20, -146) * mm, "end": v(20, -150) * mm});
            skLineSegment(sketch, "E134.1.0.0", {"start": v(40, -146) * mm, "end": v(40, -150) * mm});
            skLineSegment(sketch, "E134.2.0.0", {"start": v(60, -146) * mm, "end": v(60, -150) * mm});
            skLineSegment(sketch, "E134.3.0.0", {"start": v(80, -146) * mm, "end": v(80, -150) * mm});
            skLineSegment(sketch, "E134.4.0.0", {"start": v(100, -146) * mm, "end": v(100, -150) * mm});
            skLineSegment(sketch, "E134.direction1", {"start": v(20, -150) * mm, "end": v(40, -150) * mm, "construction": true});
            skLineSegment(sketch, "E135", {"start": v(40, -146) * mm, "end": v(60, -146) * mm});
            skLineSegment(sketch, "E136", {"start": v(80, -146) * mm, "end": v(100, -146) * mm});
            skLineSegment(sketch, "E137.trimOffspring", {"start": v(60, -150) * mm, "end": v(80, -150) * mm});
            skLineSegment(sketch, "E138.trimOffspring", {"start": v(100, -150) * mm, "end": v(120, -150) * mm});
            skSolve(sketch);
        }
        {
            var Q0;
            {var subQ0=sQuery(id+"F5.wireOp",EDGE,"E116");Q0=makeQuery(id+"F5.imprint","IMPRINT",FACE,{"disambiguationData":[TD([[makeQuery(id+"F5.imprint","IMPRINT",EDGE,{"derivedFrom":subQ0}),1.0]])]});}
            extrude(context, id + "F6", {"entities" : qUnion([Q0]), "oppositeDirection" : true, "depth" : 4 * mm});
        }
        {
            var Q0;
            Q0=makeQuery(id+"F6.opExtrude","SWEPT_BODY",BODY,{"disambiguationData":[OSD([sQuery(id+"F0.wireOp",EDGE,"E0.left"),sQuery(id+"F2.wireOp",EDGE,"E71.left"),sQuery(id+"F2.wireOp",EDGE,"E111"),sQuery(id+"F5.wireOp",EDGE,"E115"),sQuery(id+"F5.wireOp",EDGE,"E116"),sQuery(id+"F5.wireOp",EDGE,"E117"),sQuery(id+"F5.wireOp",EDGE,"E118"),sQuery(id+"F5.wireOp",EDGE,"E119"),sQuery(id+"F5.wireOp",EDGE,"E120"),sQuery(id+"F5.wireOp",EDGE,"E121"),sQuery(id+"F5.wireOp",EDGE,"E122"),sQuery(id+"F5.wireOp",EDGE,"E124"),sQuery(id+"F5.wireOp",EDGE,"E125"),sQuery(id+"F5.wireOp",EDGE,"E126"),sQuery(id+"F5.wireOp",EDGE,"E127.0.1.0"),sQuery(id+"F5.wireOp",EDGE,"E127.0.1.1"),sQuery(id+"F5.wireOp",EDGE,"E127.0.1.2"),sQuery(id+"F5.wireOp",EDGE,"E127.0.2.0"),sQuery(id+"F5.wireOp",EDGE,"E127.0.2.1"),sQuery(id+"F5.wireOp",EDGE,"E127.0.2.2"),sQuery(id+"F5.wireOp",EDGE,"E127.0.3.0"),sQuery(id+"F5.wireOp",EDGE,"E127.0.3.1"),sQuery(id+"F5.wireOp",EDGE,"E127.0.3.2"),sQuery(id+"F5.wireOp",EDGE,"E128.trimOffspring"),sQuery(id+"F5.wireOp",EDGE,"E129.trimOffspring"),sQuery(id+"F5.wireOp",EDGE,"E130.trimOffspring"),sQuery(id+"F5.wireOp",EDGE,"E131.trimOffspring"),sQuery(id+"F5.wireOp",EDGE,"E132"),sQuery(id+"F5.wireOp",EDGE,"E133"),sQuery(id+"F5.wireOp",EDGE,"E134.1.0.0"),sQuery(id+"F5.wireOp",EDGE,"E134.2.0.0"),sQuery(id+"F5.wireOp",EDGE,"E134.3.0.0"),sQuery(id+"F5.wireOp",EDGE,"E134.4.0.0"),sQuery(id+"F5.wireOp",EDGE,"E135"),sQuery(id+"F5.wireOp",EDGE,"E136"),sQuery(id+"F5.wireOp",EDGE,"E137.trimOffspring"),sQuery(id+"F5.wireOp",EDGE,"E138.trimOffspring")])]});
            transform(context, id + "F7", {"entities" : qUnion([Q0]), "transformType" : TransformType.TRANSLATION_3D, "dx" : 148 * mm, "dy" : 0 * mm, "dz" : 0 * mm, "makeCopy" : true});
        }
        {
            var Q0;
            Q0=makeQuery(id+"F1.opExtrude","SWEPT_BODY",BODY,{"disambiguationData":[OSD([sQuery(id+"F0.wireOp",EDGE,"E0.bottom"),sQuery(id+"F0.wireOp",EDGE,"E0.top"),sQuery(id+"F0.wireOp",EDGE,"E0.left"),sQuery(id+"F0.wireOp",EDGE,"E0.right"),sQuery(id+"F0.wireOp",EDGE,"E1.filletArc"),sQuery(id+"F0.wireOp",EDGE,"E2.filletArc"),sQuery(id+"F0.wireOp",EDGE,"E3"),sQuery(id+"F0.wireOp",EDGE,"E4"),sQuery(id+"F0.wireOp",EDGE,"E5"),sQuery(id+"F0.wireOp",EDGE,"E6"),sQuery(id+"F0.wireOp",EDGE,"E7"),sQuery(id+"F0.wireOp",EDGE,"E8"),sQuery(id+"F0.wireOp",EDGE,"E9"),sQuery(id+"F0.wireOp",EDGE,"E10.1.0.0"),sQuery(id+"F0.wireOp",EDGE,"E10.2.0.0"),sQuery(id+"F0.wireOp",EDGE,"E10.3.0.0"),sQuery(id+"F0.wireOp",EDGE,"E10.4.0.0"),sQuery(id+"F0.wireOp",EDGE,"E10.5.0.0"),sQuery(id+"F0.wireOp",EDGE,"E10.6.0.0"),sQuery(id+"F0.wireOp",EDGE,"E10.7.0.0"),sQuery(id+"F0.wireOp",EDGE,"E10.8.0.0"),sQuery(id+"F0.wireOp",EDGE,"E10.9.0.0"),sQuery(id+"F0.wireOp",EDGE,"E10.10.0.0"),sQuery(id+"F0.wireOp",EDGE,"E10.11.0.0"),sQuery(id+"F0.wireOp",EDGE,"E10.12.0.0"),sQuery(id+"F0.wireOp",EDGE,"E10.13.0.0"),sQuery(id+"F0.wireOp",EDGE,"E11.trimOffspring"),sQuery(id+"F0.wireOp",EDGE,"E12.trimOffspring"),sQuery(id+"F0.wireOp",EDGE,"E13.trimOffspring"),sQuery(id+"F0.wireOp",EDGE,"E14.trimOffspring"),sQuery(id+"F0.wireOp",EDGE,"E15.trimOffspring"),sQuery(id+"F0.wireOp",EDGE,"E16.trimOffspring"),sQuery(id+"F0.wireOp",EDGE,"E17.trimOffspring"),sQuery(id+"F0.wireOp",EDGE,"E18.trimOffspring"),sQuery(id+"F0.wireOp",EDGE,"E19.trimOffspring"),sQuery(id+"F0.wireOp",EDGE,"E20.trimOffspring"),sQuery(id+"F0.wireOp",EDGE,"E21.trimOffspring"),sQuery(id+"F0.wireOp",EDGE,"E22.trimOffspring"),sQuery(id+"F0.wireOp",EDGE,"E23.trimOffspring"),sQuery(id+"F0.wireOp",EDGE,"E24.trimOffspring"),sQuery(id+"F0.wireOp",EDGE,"E25"),sQuery(id+"F0.wireOp",EDGE,"E26.0.1.0"),sQuery(id+"F0.wireOp",EDGE,"E26.0.2.0"),sQuery(id+"F0.wireOp",EDGE,"E26.0.3.0"),sQuery(id+"F0.wireOp",EDGE,"E26.0.4.0"),sQuery(id+"F0.wireOp",EDGE,"E26.0.5.0"),sQuery(id+"F0.wireOp",EDGE,"E26.0.6.0"),sQuery(id+"F0.wireOp",EDGE,"E26.0.7.0"),sQuery(id+"F0.wireOp",EDGE,"E26.0.8.0"),sQuery(id+"F0.wireOp",EDGE,"E26.0.9.0"),sQuery(id+"F0.wireOp",EDGE,"E26.0.10.0"),sQuery(id+"F0.wireOp",EDGE,"E26.0.11.0"),sQuery(id+"F0.wireOp",EDGE,"E27.trimOffspring"),sQuery(id+"F0.wireOp",EDGE,"E28.trimOffspring"),sQuery(id+"F0.wireOp",EDGE,"E29.trimOffspring"),sQuery(id+"F0.wireOp",EDGE,"E30.trimOffspring"),sQuery(id+"F0.wireOp",EDGE,"E31.trimOffspring"),sQuery(id+"F0.wireOp",EDGE,"E32.trimOffspring"),sQuery(id+"F0.wireOp",EDGE,"E33.trimOffspring"),sQuery(id+"F0.wireOp",EDGE,"E34.trimOffspring"),sQuery(id+"F0.wireOp",EDGE,"E35.trimOffspring"),sQuery(id+"F0.wireOp",EDGE,"E36.trimOffspring"),sQuery(id+"F0.wireOp",EDGE,"E37.trimOffspring"),sQuery(id+"F0.wireOp",EDGE,"E38"),sQuery(id+"F0.wireOp",EDGE,"E39.1.0.0"),sQuery(id+"F0.wireOp",EDGE,"E39.2.0.0"),sQuery(id+"F0.wireOp",EDGE,"E39.3.0.0"),sQuery(id+"F0.wireOp",EDGE,"E39.4.0.0"),sQuery(id+"F0.wireOp",EDGE,"E39.5.0.0"),sQuery(id+"F0.wireOp",EDGE,"E39.6.0.0"),sQuery(id+"F0.wireOp",EDGE,"E39.7.0.0"),sQuery(id+"F0.wireOp",EDGE,"E39.8.0.0"),sQuery(id+"F0.wireOp",EDGE,"E39.9.0.0"),sQuery(id+"F0.wireOp",EDGE,"E39.10.0.0"),sQuery(id+"F0.wireOp",EDGE,"E39.11.0.0"),sQuery(id+"F0.wireOp",EDGE,"E39.12.0.0"),sQuery(id+"F0.wireOp",EDGE,"E39.13.0.0"),sQuery(id+"F0.wireOp",EDGE,"E40.trimOffspring"),sQuery(id+"F0.wireOp",EDGE,"E41.trimOffspring"),sQuery(id+"F0.wireOp",EDGE,"E42.trimOffspring"),sQuery(id+"F0.wireOp",EDGE,"E43.trimOffspring"),sQuery(id+"F0.wireOp",EDGE,"E44.trimOffspring"),sQuery(id+"F0.wireOp",EDGE,"E45.trimOffspring"),sQuery(id+"F0.wireOp",EDGE,"E46.trimOffspring"),sQuery(id+"F0.wireOp",EDGE,"E47.trimOffspring"),sQuery(id+"F0.wireOp",EDGE,"E48.trimOffspring"),sQuery(id+"F0.wireOp",EDGE,"E49.trimOffspring"),sQuery(id+"F0.wireOp",EDGE,"E50.trimOffspring"),sQuery(id+"F0.wireOp",EDGE,"E51.trimOffspring"),sQuery(id+"F0.wireOp",EDGE,"E52.trimOffspring"),sQuery(id+"F0.wireOp",EDGE,"E53.trimOffspring"),sQuery(id+"F0.wireOp",EDGE,"E54.MirrorC"),sQuery(id+"F0.wireOp",EDGE,"E55"),sQuery(id+"F0.wireOp",EDGE,"E56.0.1.0"),sQuery(id+"F0.wireOp",EDGE,"E56.0.2.0"),sQuery(id+"F0.wireOp",EDGE,"E56.0.3.0"),sQuery(id+"F0.wireOp",EDGE,"E56.0.4.0"),sQuery(id+"F0.wireOp",EDGE,"E56.0.5.0"),sQuery(id+"F0.wireOp",EDGE,"E56.0.6.0"),sQuery(id+"F0.wireOp",EDGE,"E56.0.7.0"),sQuery(id+"F0.wireOp",EDGE,"E56.0.8.0"),sQuery(id+"F0.wireOp",EDGE,"E56.0.9.0"),sQuery(id+"F0.wireOp",EDGE,"E56.0.10.0"),sQuery(id+"F0.wireOp",EDGE,"E56.0.11.0"),sQuery(id+"F0.wireOp",EDGE,"E57.trimOffspring"),sQuery(id+"F0.wireOp",EDGE,"E58.trimOffspring"),sQuery(id+"F0.wireOp",EDGE,"E59.trimOffspring"),sQuery(id+"F0.wireOp",EDGE,"E60.trimOffspring"),sQuery(id+"F0.wireOp",EDGE,"E61.trimOffspring"),sQuery(id+"F0.wireOp",EDGE,"E62.trimOffspring"),sQuery(id+"F0.wireOp",EDGE,"E63.trimOffspring"),sQuery(id+"F0.wireOp",EDGE,"E64.trimOffspring"),sQuery(id+"F0.wireOp",EDGE,"E65.trimOffspring"),sQuery(id+"F0.wireOp",EDGE,"E66.trimOffspring"),sQuery(id+"F0.wireOp",EDGE,"E67.trimOffspring"),sQuery(id+"F0.wireOp",EDGE,"E68.bottom"),sQuery(id+"F0.wireOp",EDGE,"E68.left"),sQuery(id+"F0.wireOp",EDGE,"E68.right"),sQuery(id+"F0.wireOp",EDGE,"E69.0.1.0"),sQuery(id+"F0.wireOp",EDGE,"E69.0.1.1"),sQuery(id+"F0.wireOp",EDGE,"E69.0.1.2"),sQuery(id+"F0.wireOp",EDGE,"E69.0.1.3"),sQuery(id+"F0.wireOp",EDGE,"E69.0.2.0"),sQuery(id+"F0.wireOp",EDGE,"E69.0.2.1"),sQuery(id+"F0.wireOp",EDGE,"E69.0.2.2"),sQuery(id+"F0.wireOp",EDGE,"E69.0.2.3"),sQuery(id+"F0.wireOp",EDGE,"E69.0.3.0"),sQuery(id+"F0.wireOp",EDGE,"E69.0.3.1"),sQuery(id+"F0.wireOp",EDGE,"E69.0.3.2"),sQuery(id+"F0.wireOp",EDGE,"E69.0.3.3"),sQuery(id+"F0.wireOp",EDGE,"E69.0.4.0"),sQuery(id+"F0.wireOp",EDGE,"E69.0.4.1"),sQuery(id+"F0.wireOp",EDGE,"E69.0.4.2"),sQuery(id+"F0.wireOp",EDGE,"E69.0.4.3"),sQuery(id+"F0.wireOp",EDGE,"E69.0.5.0"),sQuery(id+"F0.wireOp",EDGE,"E69.0.5.1"),sQuery(id+"F0.wireOp",EDGE,"E69.0.5.2"),sQuery(id+"F0.wireOp",EDGE,"E69.0.5.3"),sQuery(id+"F0.wireOp",EDGE,"E70.trimOffspring")])]});
            var Q1;
            Q1=makeQuery(id+"F3.opExtrude","SWEPT_BODY",BODY,{"disambiguationData":[OSD([sQuery(id+"F2.wireOp",EDGE,"E71.bottom"),sQuery(id+"F2.wireOp",EDGE,"E71.top"),sQuery(id+"F2.wireOp",EDGE,"E71.left"),sQuery(id+"F2.wireOp",EDGE,"E71.right"),sQuery(id+"F2.wireOp",EDGE,"E72.filletArc"),sQuery(id+"F2.wireOp",EDGE,"E73.filletArc"),sQuery(id+"F2.wireOp",EDGE,"E74"),sQuery(id+"F2.wireOp",EDGE,"E75"),sQuery(id+"F2.wireOp",EDGE,"E76"),sQuery(id+"F2.wireOp",EDGE,"E77"),sQuery(id+"F2.wireOp",EDGE,"E80"),sQuery(id+"F2.wireOp",EDGE,"E81"),sQuery(id+"F2.wireOp",EDGE,"E82.trimOffspring"),sQuery(id+"F2.wireOp",EDGE,"E83.filletArc"),sQuery(id+"F2.wireOp",EDGE,"E84.filletArc"),sQuery(id+"F2.wireOp",EDGE,"E85.filletArc"),sQuery(id+"F2.wireOp",EDGE,"E86.filletArc"),sQuery(id+"F2.wireOp",EDGE,"E87"),sQuery(id+"F2.wireOp",EDGE,"E88"),sQuery(id+"F2.wireOp",EDGE,"E89.trimOffspring"),sQuery(id+"F2.wireOp",EDGE,"E90"),sQuery(id+"F2.wireOp",EDGE,"E91"),sQuery(id+"F2.wireOp",EDGE,"E92"),sQuery(id+"F2.wireOp",EDGE,"E93"),sQuery(id+"F2.wireOp",EDGE,"E94.trimOffspring"),sQuery(id+"F2.wireOp",EDGE,"E95.trimOffspring"),sQuery(id+"F2.wireOp",EDGE,"E96.filletArc"),sQuery(id+"F2.wireOp",EDGE,"E97.filletArc"),sQuery(id+"F2.wireOp",EDGE,"E98.filletArc"),sQuery(id+"F2.wireOp",EDGE,"E99.filletArc"),sQuery(id+"F2.wireOp",EDGE,"E100.filletArc"),sQuery(id+"F2.wireOp",EDGE,"E101.filletArc"),sQuery(id+"F2.wireOp",EDGE,"E102.filletArc"),sQuery(id+"F2.wireOp",EDGE,"E103.filletArc"),sQuery(id+"F2.wireOp",EDGE,"E104.filletArc"),sQuery(id+"F2.wireOp",EDGE,"E105.filletArc"),sQuery(id+"F2.wireOp",EDGE,"E106.filletArc"),sQuery(id+"F2.wireOp",EDGE,"E107.filletArc"),sQuery(id+"F2.wireOp",EDGE,"E108.bottom"),sQuery(id+"F2.wireOp",EDGE,"E108.top"),sQuery(id+"F2.wireOp",EDGE,"E108.left"),sQuery(id+"F2.wireOp",EDGE,"E108.right"),sQuery(id+"F2.wireOp",EDGE,"E109"),sQuery(id+"F2.wireOp",EDGE,"E110"),sQuery(id+"F2.wireOp",EDGE,"E111"),sQuery(id+"F2.wireOp",EDGE,"E112"),sQuery(id+"F2.wireOp",EDGE,"E113"),sQuery(id+"F2.wireOp",EDGE,"E114")])]});
            var Q2;
            Q2=makeQuery(id+"F6.opExtrude","SWEPT_BODY",BODY,{"disambiguationData":[OSD([sQuery(id+"F0.wireOp",EDGE,"E0.left"),sQuery(id+"F2.wireOp",EDGE,"E71.left"),sQuery(id+"F2.wireOp",EDGE,"E111"),sQuery(id+"F5.wireOp",EDGE,"E115"),sQuery(id+"F5.wireOp",EDGE,"E116"),sQuery(id+"F5.wireOp",EDGE,"E117"),sQuery(id+"F5.wireOp",EDGE,"E118"),sQuery(id+"F5.wireOp",EDGE,"E119"),sQuery(id+"F5.wireOp",EDGE,"E120"),sQuery(id+"F5.wireOp",EDGE,"E121"),sQuery(id+"F5.wireOp",EDGE,"E122"),sQuery(id+"F5.wireOp",EDGE,"E124"),sQuery(id+"F5.wireOp",EDGE,"E125"),sQuery(id+"F5.wireOp",EDGE,"E126"),sQuery(id+"F5.wireOp",EDGE,"E127.0.1.0"),sQuery(id+"F5.wireOp",EDGE,"E127.0.1.1"),sQuery(id+"F5.wireOp",EDGE,"E127.0.1.2"),sQuery(id+"F5.wireOp",EDGE,"E127.0.2.0"),sQuery(id+"F5.wireOp",EDGE,"E127.0.2.1"),sQuery(id+"F5.wireOp",EDGE,"E127.0.2.2"),sQuery(id+"F5.wireOp",EDGE,"E127.0.3.0"),sQuery(id+"F5.wireOp",EDGE,"E127.0.3.1"),sQuery(id+"F5.wireOp",EDGE,"E127.0.3.2"),sQuery(id+"F5.wireOp",EDGE,"E128.trimOffspring"),sQuery(id+"F5.wireOp",EDGE,"E129.trimOffspring"),sQuery(id+"F5.wireOp",EDGE,"E130.trimOffspring"),sQuery(id+"F5.wireOp",EDGE,"E131.trimOffspring"),sQuery(id+"F5.wireOp",EDGE,"E132"),sQuery(id+"F5.wireOp",EDGE,"E133"),sQuery(id+"F5.wireOp",EDGE,"E134.1.0.0"),sQuery(id+"F5.wireOp",EDGE,"E134.2.0.0"),sQuery(id+"F5.wireOp",EDGE,"E134.3.0.0"),sQuery(id+"F5.wireOp",EDGE,"E134.4.0.0"),sQuery(id+"F5.wireOp",EDGE,"E135"),sQuery(id+"F5.wireOp",EDGE,"E136"),sQuery(id+"F5.wireOp",EDGE,"E137.trimOffspring"),sQuery(id+"F5.wireOp",EDGE,"E138.trimOffspring")])]});
            booleanBodies(context, id + "F8", {"operationType" : BooleanOperationType.SUBTRACTION, "tools" : qUnion([Q0, Q1]), "targets" : qUnion([Q2]), "keepTools" : true});
        }
        {
            var Q0;
            Q0=makeQuery(id+"F6.opExtrude","SWEPT_BODY",BODY,{"disambiguationData":[OSD([sQuery(id+"F0.wireOp",EDGE,"E0.left"),sQuery(id+"F2.wireOp",EDGE,"E71.left"),sQuery(id+"F2.wireOp",EDGE,"E111"),sQuery(id+"F5.wireOp",EDGE,"E115"),sQuery(id+"F5.wireOp",EDGE,"E116"),sQuery(id+"F5.wireOp",EDGE,"E117"),sQuery(id+"F5.wireOp",EDGE,"E118"),sQuery(id+"F5.wireOp",EDGE,"E119"),sQuery(id+"F5.wireOp",EDGE,"E120"),sQuery(id+"F5.wireOp",EDGE,"E121"),sQuery(id+"F5.wireOp",EDGE,"E122"),sQuery(id+"F5.wireOp",EDGE,"E124"),sQuery(id+"F5.wireOp",EDGE,"E125"),sQuery(id+"F5.wireOp",EDGE,"E126"),sQuery(id+"F5.wireOp",EDGE,"E127.0.1.0"),sQuery(id+"F5.wireOp",EDGE,"E127.0.1.1"),sQuery(id+"F5.wireOp",EDGE,"E127.0.1.2"),sQuery(id+"F5.wireOp",EDGE,"E127.0.2.0"),sQuery(id+"F5.wireOp",EDGE,"E127.0.2.1"),sQuery(id+"F5.wireOp",EDGE,"E127.0.2.2"),sQuery(id+"F5.wireOp",EDGE,"E127.0.3.0"),sQuery(id+"F5.wireOp",EDGE,"E127.0.3.1"),sQuery(id+"F5.wireOp",EDGE,"E127.0.3.2"),sQuery(id+"F5.wireOp",EDGE,"E128.trimOffspring"),sQuery(id+"F5.wireOp",EDGE,"E129.trimOffspring"),sQuery(id+"F5.wireOp",EDGE,"E130.trimOffspring"),sQuery(id+"F5.wireOp",EDGE,"E131.trimOffspring"),sQuery(id+"F5.wireOp",EDGE,"E132"),sQuery(id+"F5.wireOp",EDGE,"E133"),sQuery(id+"F5.wireOp",EDGE,"E134.1.0.0"),sQuery(id+"F5.wireOp",EDGE,"E134.2.0.0"),sQuery(id+"F5.wireOp",EDGE,"E134.3.0.0"),sQuery(id+"F5.wireOp",EDGE,"E134.4.0.0"),sQuery(id+"F5.wireOp",EDGE,"E135"),sQuery(id+"F5.wireOp",EDGE,"E136"),sQuery(id+"F5.wireOp",EDGE,"E137.trimOffspring"),sQuery(id+"F5.wireOp",EDGE,"E138.trimOffspring")])]});
            transform(context, id + "F9", {"entities" : qUnion([Q0]), "transformType" : TransformType.TRANSLATION_3D, "dx" : 296 * mm, "dy" : 0 * mm, "dz" : 0 * mm, "makeCopy" : true});
        }
        {
            var Q0;
            Q0=makeQuery(id+"F1.opExtrude","SWEPT_BODY",BODY,{"disambiguationData":[OSD([sQuery(id+"F0.wireOp",EDGE,"E0.bottom"),sQuery(id+"F0.wireOp",EDGE,"E0.top"),sQuery(id+"F0.wireOp",EDGE,"E0.left"),sQuery(id+"F0.wireOp",EDGE,"E0.right"),sQuery(id+"F0.wireOp",EDGE,"E1.filletArc"),sQuery(id+"F0.wireOp",EDGE,"E2.filletArc"),sQuery(id+"F0.wireOp",EDGE,"E3"),sQuery(id+"F0.wireOp",EDGE,"E4"),sQuery(id+"F0.wireOp",EDGE,"E5"),sQuery(id+"F0.wireOp",EDGE,"E6"),sQuery(id+"F0.wireOp",EDGE,"E7"),sQuery(id+"F0.wireOp",EDGE,"E8"),sQuery(id+"F0.wireOp",EDGE,"E9"),sQuery(id+"F0.wireOp",EDGE,"E10.1.0.0"),sQuery(id+"F0.wireOp",EDGE,"E10.2.0.0"),sQuery(id+"F0.wireOp",EDGE,"E10.3.0.0"),sQuery(id+"F0.wireOp",EDGE,"E10.4.0.0"),sQuery(id+"F0.wireOp",EDGE,"E10.5.0.0"),sQuery(id+"F0.wireOp",EDGE,"E10.6.0.0"),sQuery(id+"F0.wireOp",EDGE,"E10.7.0.0"),sQuery(id+"F0.wireOp",EDGE,"E10.8.0.0"),sQuery(id+"F0.wireOp",EDGE,"E10.9.0.0"),sQuery(id+"F0.wireOp",EDGE,"E10.10.0.0"),sQuery(id+"F0.wireOp",EDGE,"E10.11.0.0"),sQuery(id+"F0.wireOp",EDGE,"E10.12.0.0"),sQuery(id+"F0.wireOp",EDGE,"E10.13.0.0"),sQuery(id+"F0.wireOp",EDGE,"E11.trimOffspring"),sQuery(id+"F0.wireOp",EDGE,"E12.trimOffspring"),sQuery(id+"F0.wireOp",EDGE,"E13.trimOffspring"),sQuery(id+"F0.wireOp",EDGE,"E14.trimOffspring"),sQuery(id+"F0.wireOp",EDGE,"E15.trimOffspring"),sQuery(id+"F0.wireOp",EDGE,"E16.trimOffspring"),sQuery(id+"F0.wireOp",EDGE,"E17.trimOffspring"),sQuery(id+"F0.wireOp",EDGE,"E18.trimOffspring"),sQuery(id+"F0.wireOp",EDGE,"E19.trimOffspring"),sQuery(id+"F0.wireOp",EDGE,"E20.trimOffspring"),sQuery(id+"F0.wireOp",EDGE,"E21.trimOffspring"),sQuery(id+"F0.wireOp",EDGE,"E22.trimOffspring"),sQuery(id+"F0.wireOp",EDGE,"E23.trimOffspring"),sQuery(id+"F0.wireOp",EDGE,"E24.trimOffspring"),sQuery(id+"F0.wireOp",EDGE,"E25"),sQuery(id+"F0.wireOp",EDGE,"E26.0.1.0"),sQuery(id+"F0.wireOp",EDGE,"E26.0.2.0"),sQuery(id+"F0.wireOp",EDGE,"E26.0.3.0"),sQuery(id+"F0.wireOp",EDGE,"E26.0.4.0"),sQuery(id+"F0.wireOp",EDGE,"E26.0.5.0"),sQuery(id+"F0.wireOp",EDGE,"E26.0.6.0"),sQuery(id+"F0.wireOp",EDGE,"E26.0.7.0"),sQuery(id+"F0.wireOp",EDGE,"E26.0.8.0"),sQuery(id+"F0.wireOp",EDGE,"E26.0.9.0"),sQuery(id+"F0.wireOp",EDGE,"E26.0.10.0"),sQuery(id+"F0.wireOp",EDGE,"E26.0.11.0"),sQuery(id+"F0.wireOp",EDGE,"E27.trimOffspring"),sQuery(id+"F0.wireOp",EDGE,"E28.trimOffspring"),sQuery(id+"F0.wireOp",EDGE,"E29.trimOffspring"),sQuery(id+"F0.wireOp",EDGE,"E30.trimOffspring"),sQuery(id+"F0.wireOp",EDGE,"E31.trimOffspring"),sQuery(id+"F0.wireOp",EDGE,"E32.trimOffspring"),sQuery(id+"F0.wireOp",EDGE,"E33.trimOffspring"),sQuery(id+"F0.wireOp",EDGE,"E34.trimOffspring"),sQuery(id+"F0.wireOp",EDGE,"E35.trimOffspring"),sQuery(id+"F0.wireOp",EDGE,"E36.trimOffspring"),sQuery(id+"F0.wireOp",EDGE,"E37.trimOffspring"),sQuery(id+"F0.wireOp",EDGE,"E38"),sQuery(id+"F0.wireOp",EDGE,"E39.1.0.0"),sQuery(id+"F0.wireOp",EDGE,"E39.2.0.0"),sQuery(id+"F0.wireOp",EDGE,"E39.3.0.0"),sQuery(id+"F0.wireOp",EDGE,"E39.4.0.0"),sQuery(id+"F0.wireOp",EDGE,"E39.5.0.0"),sQuery(id+"F0.wireOp",EDGE,"E39.6.0.0"),sQuery(id+"F0.wireOp",EDGE,"E39.7.0.0"),sQuery(id+"F0.wireOp",EDGE,"E39.8.0.0"),sQuery(id+"F0.wireOp",EDGE,"E39.9.0.0"),sQuery(id+"F0.wireOp",EDGE,"E39.10.0.0"),sQuery(id+"F0.wireOp",EDGE,"E39.11.0.0"),sQuery(id+"F0.wireOp",EDGE,"E39.12.0.0"),sQuery(id+"F0.wireOp",EDGE,"E39.13.0.0"),sQuery(id+"F0.wireOp",EDGE,"E40.trimOffspring"),sQuery(id+"F0.wireOp",EDGE,"E41.trimOffspring"),sQuery(id+"F0.wireOp",EDGE,"E42.trimOffspring"),sQuery(id+"F0.wireOp",EDGE,"E43.trimOffspring"),sQuery(id+"F0.wireOp",EDGE,"E44.trimOffspring"),sQuery(id+"F0.wireOp",EDGE,"E45.trimOffspring"),sQuery(id+"F0.wireOp",EDGE,"E46.trimOffspring"),sQuery(id+"F0.wireOp",EDGE,"E47.trimOffspring"),sQuery(id+"F0.wireOp",EDGE,"E48.trimOffspring"),sQuery(id+"F0.wireOp",EDGE,"E49.trimOffspring"),sQuery(id+"F0.wireOp",EDGE,"E50.trimOffspring"),sQuery(id+"F0.wireOp",EDGE,"E51.trimOffspring"),sQuery(id+"F0.wireOp",EDGE,"E52.trimOffspring"),sQuery(id+"F0.wireOp",EDGE,"E53.trimOffspring"),sQuery(id+"F0.wireOp",EDGE,"E54.MirrorC"),sQuery(id+"F0.wireOp",EDGE,"E55"),sQuery(id+"F0.wireOp",EDGE,"E56.0.1.0"),sQuery(id+"F0.wireOp",EDGE,"E56.0.2.0"),sQuery(id+"F0.wireOp",EDGE,"E56.0.3.0"),sQuery(id+"F0.wireOp",EDGE,"E56.0.4.0"),sQuery(id+"F0.wireOp",EDGE,"E56.0.5.0"),sQuery(id+"F0.wireOp",EDGE,"E56.0.6.0"),sQuery(id+"F0.wireOp",EDGE,"E56.0.7.0"),sQuery(id+"F0.wireOp",EDGE,"E56.0.8.0"),sQuery(id+"F0.wireOp",EDGE,"E56.0.9.0"),sQuery(id+"F0.wireOp",EDGE,"E56.0.10.0"),sQuery(id+"F0.wireOp",EDGE,"E56.0.11.0"),sQuery(id+"F0.wireOp",EDGE,"E57.trimOffspring"),sQuery(id+"F0.wireOp",EDGE,"E58.trimOffspring"),sQuery(id+"F0.wireOp",EDGE,"E59.trimOffspring"),sQuery(id+"F0.wireOp",EDGE,"E60.trimOffspring"),sQuery(id+"F0.wireOp",EDGE,"E61.trimOffspring"),sQuery(id+"F0.wireOp",EDGE,"E62.trimOffspring"),sQuery(id+"F0.wireOp",EDGE,"E63.trimOffspring"),sQuery(id+"F0.wireOp",EDGE,"E64.trimOffspring"),sQuery(id+"F0.wireOp",EDGE,"E65.trimOffspring"),sQuery(id+"F0.wireOp",EDGE,"E66.trimOffspring"),sQuery(id+"F0.wireOp",EDGE,"E67.trimOffspring"),sQuery(id+"F0.wireOp",EDGE,"E68.bottom"),sQuery(id+"F0.wireOp",EDGE,"E68.left"),sQuery(id+"F0.wireOp",EDGE,"E68.right"),sQuery(id+"F0.wireOp",EDGE,"E69.0.1.0"),sQuery(id+"F0.wireOp",EDGE,"E69.0.1.1"),sQuery(id+"F0.wireOp",EDGE,"E69.0.1.2"),sQuery(id+"F0.wireOp",EDGE,"E69.0.1.3"),sQuery(id+"F0.wireOp",EDGE,"E69.0.2.0"),sQuery(id+"F0.wireOp",EDGE,"E69.0.2.1"),sQuery(id+"F0.wireOp",EDGE,"E69.0.2.2"),sQuery(id+"F0.wireOp",EDGE,"E69.0.2.3"),sQuery(id+"F0.wireOp",EDGE,"E69.0.3.0"),sQuery(id+"F0.wireOp",EDGE,"E69.0.3.1"),sQuery(id+"F0.wireOp",EDGE,"E69.0.3.2"),sQuery(id+"F0.wireOp",EDGE,"E69.0.3.3"),sQuery(id+"F0.wireOp",EDGE,"E69.0.4.0"),sQuery(id+"F0.wireOp",EDGE,"E69.0.4.1"),sQuery(id+"F0.wireOp",EDGE,"E69.0.4.2"),sQuery(id+"F0.wireOp",EDGE,"E69.0.4.3"),sQuery(id+"F0.wireOp",EDGE,"E69.0.5.0"),sQuery(id+"F0.wireOp",EDGE,"E69.0.5.1"),sQuery(id+"F0.wireOp",EDGE,"E69.0.5.2"),sQuery(id+"F0.wireOp",EDGE,"E69.0.5.3"),sQuery(id+"F0.wireOp",EDGE,"E70.trimOffspring")])]});
            var Q1;
            Q1=makeQuery(id+"F3.opExtrude","SWEPT_BODY",BODY,{"disambiguationData":[OSD([sQuery(id+"F2.wireOp",EDGE,"E71.bottom"),sQuery(id+"F2.wireOp",EDGE,"E71.top"),sQuery(id+"F2.wireOp",EDGE,"E71.left"),sQuery(id+"F2.wireOp",EDGE,"E71.right"),sQuery(id+"F2.wireOp",EDGE,"E72.filletArc"),sQuery(id+"F2.wireOp",EDGE,"E73.filletArc"),sQuery(id+"F2.wireOp",EDGE,"E74"),sQuery(id+"F2.wireOp",EDGE,"E75"),sQuery(id+"F2.wireOp",EDGE,"E76"),sQuery(id+"F2.wireOp",EDGE,"E77"),sQuery(id+"F2.wireOp",EDGE,"E80"),sQuery(id+"F2.wireOp",EDGE,"E81"),sQuery(id+"F2.wireOp",EDGE,"E82.trimOffspring"),sQuery(id+"F2.wireOp",EDGE,"E83.filletArc"),sQuery(id+"F2.wireOp",EDGE,"E84.filletArc"),sQuery(id+"F2.wireOp",EDGE,"E85.filletArc"),sQuery(id+"F2.wireOp",EDGE,"E86.filletArc"),sQuery(id+"F2.wireOp",EDGE,"E87"),sQuery(id+"F2.wireOp",EDGE,"E88"),sQuery(id+"F2.wireOp",EDGE,"E89.trimOffspring"),sQuery(id+"F2.wireOp",EDGE,"E90"),sQuery(id+"F2.wireOp",EDGE,"E91"),sQuery(id+"F2.wireOp",EDGE,"E92"),sQuery(id+"F2.wireOp",EDGE,"E93"),sQuery(id+"F2.wireOp",EDGE,"E94.trimOffspring"),sQuery(id+"F2.wireOp",EDGE,"E95.trimOffspring"),sQuery(id+"F2.wireOp",EDGE,"E96.filletArc"),sQuery(id+"F2.wireOp",EDGE,"E97.filletArc"),sQuery(id+"F2.wireOp",EDGE,"E98.filletArc"),sQuery(id+"F2.wireOp",EDGE,"E99.filletArc"),sQuery(id+"F2.wireOp",EDGE,"E100.filletArc"),sQuery(id+"F2.wireOp",EDGE,"E101.filletArc"),sQuery(id+"F2.wireOp",EDGE,"E102.filletArc"),sQuery(id+"F2.wireOp",EDGE,"E103.filletArc"),sQuery(id+"F2.wireOp",EDGE,"E104.filletArc"),sQuery(id+"F2.wireOp",EDGE,"E105.filletArc"),sQuery(id+"F2.wireOp",EDGE,"E106.filletArc"),sQuery(id+"F2.wireOp",EDGE,"E107.filletArc"),sQuery(id+"F2.wireOp",EDGE,"E108.bottom"),sQuery(id+"F2.wireOp",EDGE,"E108.top"),sQuery(id+"F2.wireOp",EDGE,"E108.left"),sQuery(id+"F2.wireOp",EDGE,"E108.right"),sQuery(id+"F2.wireOp",EDGE,"E109"),sQuery(id+"F2.wireOp",EDGE,"E110"),sQuery(id+"F2.wireOp",EDGE,"E111"),sQuery(id+"F2.wireOp",EDGE,"E112"),sQuery(id+"F2.wireOp",EDGE,"E113"),sQuery(id+"F2.wireOp",EDGE,"E114")])]});
            var Q2;
            Q2=makeQuery(id+"F7.opPattern","COPY",BODY,{"derivedFrom":makeQuery(id+"F6.opExtrude","SWEPT_BODY",BODY,{"disambiguationData":[OSD([sQuery(id+"F0.wireOp",EDGE,"E0.left"),sQuery(id+"F2.wireOp",EDGE,"E71.left"),sQuery(id+"F2.wireOp",EDGE,"E111"),sQuery(id+"F5.wireOp",EDGE,"E115"),sQuery(id+"F5.wireOp",EDGE,"E116"),sQuery(id+"F5.wireOp",EDGE,"E117"),sQuery(id+"F5.wireOp",EDGE,"E118"),sQuery(id+"F5.wireOp",EDGE,"E119"),sQuery(id+"F5.wireOp",EDGE,"E120"),sQuery(id+"F5.wireOp",EDGE,"E121"),sQuery(id+"F5.wireOp",EDGE,"E122"),sQuery(id+"F5.wireOp",EDGE,"E124"),sQuery(id+"F5.wireOp",EDGE,"E125"),sQuery(id+"F5.wireOp",EDGE,"E126"),sQuery(id+"F5.wireOp",EDGE,"E127.0.1.0"),sQuery(id+"F5.wireOp",EDGE,"E127.0.1.1"),sQuery(id+"F5.wireOp",EDGE,"E127.0.1.2"),sQuery(id+"F5.wireOp",EDGE,"E127.0.2.0"),sQuery(id+"F5.wireOp",EDGE,"E127.0.2.1"),sQuery(id+"F5.wireOp",EDGE,"E127.0.2.2"),sQuery(id+"F5.wireOp",EDGE,"E127.0.3.0"),sQuery(id+"F5.wireOp",EDGE,"E127.0.3.1"),sQuery(id+"F5.wireOp",EDGE,"E127.0.3.2"),sQuery(id+"F5.wireOp",EDGE,"E128.trimOffspring"),sQuery(id+"F5.wireOp",EDGE,"E129.trimOffspring"),sQuery(id+"F5.wireOp",EDGE,"E130.trimOffspring"),sQuery(id+"F5.wireOp",EDGE,"E131.trimOffspring"),sQuery(id+"F5.wireOp",EDGE,"E132"),sQuery(id+"F5.wireOp",EDGE,"E133"),sQuery(id+"F5.wireOp",EDGE,"E134.1.0.0"),sQuery(id+"F5.wireOp",EDGE,"E134.2.0.0"),sQuery(id+"F5.wireOp",EDGE,"E134.3.0.0"),sQuery(id+"F5.wireOp",EDGE,"E134.4.0.0"),sQuery(id+"F5.wireOp",EDGE,"E135"),sQuery(id+"F5.wireOp",EDGE,"E136"),sQuery(id+"F5.wireOp",EDGE,"E137.trimOffspring"),sQuery(id+"F5.wireOp",EDGE,"E138.trimOffspring")])]}),"instanceName":"1"});
            booleanBodies(context, id + "F10", {"operationType" : BooleanOperationType.SUBTRACTION, "tools" : qUnion([Q0, Q1]), "targets" : qUnion([Q2]), "keepTools" : true});
        }
        {
            var Q0;
            Q0=makeQuery(id+"F1.opExtrude","SWEPT_FACE",FACE,{"disambiguationData":[OSD([sQuery(id+"F0.wireOp",EDGE,"E45.trimOffspring")])]});
            var sketch = newSketch(context, id + "F11", { "sketchPlane" : qUnion([Q0])});
            skLineSegment(sketch, "E139.bottom", {"start": v(-150, 0) * mm, "end": v(150, 0) * mm});
            skLineSegment(sketch, "E139.top", {"start": v(-150, 120) * mm, "end": v(-130, 120) * mm});
            skLineSegment(sketch, "E139.left", {"start": v(-150, 0) * mm, "end": v(-150, 120) * mm});
            skLineSegment(sketch, "E139.right", {"start": v(150, 0) * mm, "end": v(150, 120) * mm});
            skLineSegment(sketch, "E140", {"start": v(-130, 116) * mm, "end": v(-110, 116) * mm});
            skLineSegment(sketch, "E141", {"start": v(-130, 120) * mm, "end": v(-130, 116) * mm});
            skLineSegment(sketch, "E142.1.0.0", {"start": v(-110, 120) * mm, "end": v(-110, 116) * mm});
            skLineSegment(sketch, "E142.2.0.0", {"start": v(-90, 120) * mm, "end": v(-90, 116) * mm});
            skLineSegment(sketch, "E142.3.0.0", {"start": v(-70, 120) * mm, "end": v(-70, 116) * mm});
            skLineSegment(sketch, "E142.4.0.0", {"start": v(-50, 120) * mm, "end": v(-50, 116) * mm});
            skLineSegment(sketch, "E142.5.0.0", {"start": v(-30, 120) * mm, "end": v(-30, 116) * mm});
            skLineSegment(sketch, "E142.6.0.0", {"start": v(-10, 120) * mm, "end": v(-10, 116) * mm});
            skLineSegment(sketch, "E142.7.0.0", {"start": v(10, 120) * mm, "end": v(10, 116) * mm});
            skLineSegment(sketch, "E142.8.0.0", {"start": v(30, 120) * mm, "end": v(30, 116) * mm});
            skLineSegment(sketch, "E142.9.0.0", {"start": v(50, 120) * mm, "end": v(50, 116) * mm});
            skLineSegment(sketch, "E142.10.0.0", {"start": v(70, 120) * mm, "end": v(70, 116) * mm});
            skLineSegment(sketch, "E142.11.0.0", {"start": v(90, 120) * mm, "end": v(90, 116) * mm});
            skLineSegment(sketch, "E142.12.0.0", {"start": v(110, 120) * mm, "end": v(110, 116) * mm});
            skLineSegment(sketch, "E142.13.0.0", {"start": v(130, 120) * mm, "end": v(130, 116) * mm});
            skLineSegment(sketch, "E142.direction1", {"start": v(-130, 116) * mm, "end": v(-110, 116) * mm, "construction": true});
            skLineSegment(sketch, "E143.trimOffspring", {"start": v(-110, 120) * mm, "end": v(-90, 120) * mm});
            skLineSegment(sketch, "E144.trimOffspring", {"start": v(-90, 116) * mm, "end": v(-70, 116) * mm});
            skLineSegment(sketch, "E145.trimOffspring", {"start": v(-70, 120) * mm, "end": v(-50, 120) * mm});
            skLineSegment(sketch, "E146.trimOffspring", {"start": v(-30, 120) * mm, "end": v(-10, 120) * mm});
            skLineSegment(sketch, "E147.trimOffspring", {"start": v(-10, 116) * mm, "end": v(10, 116) * mm});
            skLineSegment(sketch, "E148.trimOffspring", {"start": v(10, 120) * mm, "end": v(30, 120) * mm});
            skLineSegment(sketch, "E149.trimOffspring", {"start": v(-50, 116) * mm, "end": v(-30, 116) * mm});
            skLineSegment(sketch, "E150.trimOffspring", {"start": v(30, 116) * mm, "end": v(50, 116) * mm});
            skLineSegment(sketch, "E151.trimOffspring", {"start": v(50, 120) * mm, "end": v(70, 120) * mm});
            skLineSegment(sketch, "E152.trimOffspring", {"start": v(70, 116) * mm, "end": v(90, 116) * mm});
            skLineSegment(sketch, "E153.trimOffspring", {"start": v(90, 120) * mm, "end": v(110, 120) * mm});
            skLineSegment(sketch, "E154.trimOffspring", {"start": v(110, 116) * mm, "end": v(130, 116) * mm});
            skLineSegment(sketch, "E155.trimOffspring", {"start": v(130, 120) * mm, "end": v(150, 120) * mm});
            skSolve(sketch);
        }
        {
            var Q0;
            Q0 = qSketchRegion(id + "F11", true);
            extrude(context, id + "F12", {"entities" : qUnion([Q0]), "oppositeDirection" : true, "depth" : 4 * mm});
        }
        {
            var Q0;
            Q0=makeQuery(id+"F1.opExtrude","SWEPT_BODY",BODY,{"disambiguationData":[OSD([sQuery(id+"F0.wireOp",EDGE,"E0.bottom"),sQuery(id+"F0.wireOp",EDGE,"E0.top"),sQuery(id+"F0.wireOp",EDGE,"E0.left"),sQuery(id+"F0.wireOp",EDGE,"E0.right"),sQuery(id+"F0.wireOp",EDGE,"E1.filletArc"),sQuery(id+"F0.wireOp",EDGE,"E2.filletArc"),sQuery(id+"F0.wireOp",EDGE,"E3"),sQuery(id+"F0.wireOp",EDGE,"E4"),sQuery(id+"F0.wireOp",EDGE,"E5"),sQuery(id+"F0.wireOp",EDGE,"E6"),sQuery(id+"F0.wireOp",EDGE,"E7"),sQuery(id+"F0.wireOp",EDGE,"E8"),sQuery(id+"F0.wireOp",EDGE,"E9"),sQuery(id+"F0.wireOp",EDGE,"E10.1.0.0"),sQuery(id+"F0.wireOp",EDGE,"E10.2.0.0"),sQuery(id+"F0.wireOp",EDGE,"E10.3.0.0"),sQuery(id+"F0.wireOp",EDGE,"E10.4.0.0"),sQuery(id+"F0.wireOp",EDGE,"E10.5.0.0"),sQuery(id+"F0.wireOp",EDGE,"E10.6.0.0"),sQuery(id+"F0.wireOp",EDGE,"E10.7.0.0"),sQuery(id+"F0.wireOp",EDGE,"E10.8.0.0"),sQuery(id+"F0.wireOp",EDGE,"E10.9.0.0"),sQuery(id+"F0.wireOp",EDGE,"E10.10.0.0"),sQuery(id+"F0.wireOp",EDGE,"E10.11.0.0"),sQuery(id+"F0.wireOp",EDGE,"E10.12.0.0"),sQuery(id+"F0.wireOp",EDGE,"E10.13.0.0"),sQuery(id+"F0.wireOp",EDGE,"E11.trimOffspring"),sQuery(id+"F0.wireOp",EDGE,"E12.trimOffspring"),sQuery(id+"F0.wireOp",EDGE,"E13.trimOffspring"),sQuery(id+"F0.wireOp",EDGE,"E14.trimOffspring"),sQuery(id+"F0.wireOp",EDGE,"E15.trimOffspring"),sQuery(id+"F0.wireOp",EDGE,"E16.trimOffspring"),sQuery(id+"F0.wireOp",EDGE,"E17.trimOffspring"),sQuery(id+"F0.wireOp",EDGE,"E18.trimOffspring"),sQuery(id+"F0.wireOp",EDGE,"E19.trimOffspring"),sQuery(id+"F0.wireOp",EDGE,"E20.trimOffspring"),sQuery(id+"F0.wireOp",EDGE,"E21.trimOffspring"),sQuery(id+"F0.wireOp",EDGE,"E22.trimOffspring"),sQuery(id+"F0.wireOp",EDGE,"E23.trimOffspring"),sQuery(id+"F0.wireOp",EDGE,"E24.trimOffspring"),sQuery(id+"F0.wireOp",EDGE,"E25"),sQuery(id+"F0.wireOp",EDGE,"E26.0.1.0"),sQuery(id+"F0.wireOp",EDGE,"E26.0.2.0"),sQuery(id+"F0.wireOp",EDGE,"E26.0.3.0"),sQuery(id+"F0.wireOp",EDGE,"E26.0.4.0"),sQuery(id+"F0.wireOp",EDGE,"E26.0.5.0"),sQuery(id+"F0.wireOp",EDGE,"E26.0.6.0"),sQuery(id+"F0.wireOp",EDGE,"E26.0.7.0"),sQuery(id+"F0.wireOp",EDGE,"E26.0.8.0"),sQuery(id+"F0.wireOp",EDGE,"E26.0.9.0"),sQuery(id+"F0.wireOp",EDGE,"E26.0.10.0"),sQuery(id+"F0.wireOp",EDGE,"E26.0.11.0"),sQuery(id+"F0.wireOp",EDGE,"E27.trimOffspring"),sQuery(id+"F0.wireOp",EDGE,"E28.trimOffspring"),sQuery(id+"F0.wireOp",EDGE,"E29.trimOffspring"),sQuery(id+"F0.wireOp",EDGE,"E30.trimOffspring"),sQuery(id+"F0.wireOp",EDGE,"E31.trimOffspring"),sQuery(id+"F0.wireOp",EDGE,"E32.trimOffspring"),sQuery(id+"F0.wireOp",EDGE,"E33.trimOffspring"),sQuery(id+"F0.wireOp",EDGE,"E34.trimOffspring"),sQuery(id+"F0.wireOp",EDGE,"E35.trimOffspring"),sQuery(id+"F0.wireOp",EDGE,"E36.trimOffspring"),sQuery(id+"F0.wireOp",EDGE,"E37.trimOffspring"),sQuery(id+"F0.wireOp",EDGE,"E38"),sQuery(id+"F0.wireOp",EDGE,"E39.1.0.0"),sQuery(id+"F0.wireOp",EDGE,"E39.2.0.0"),sQuery(id+"F0.wireOp",EDGE,"E39.3.0.0"),sQuery(id+"F0.wireOp",EDGE,"E39.4.0.0"),sQuery(id+"F0.wireOp",EDGE,"E39.5.0.0"),sQuery(id+"F0.wireOp",EDGE,"E39.6.0.0"),sQuery(id+"F0.wireOp",EDGE,"E39.7.0.0"),sQuery(id+"F0.wireOp",EDGE,"E39.8.0.0"),sQuery(id+"F0.wireOp",EDGE,"E39.9.0.0"),sQuery(id+"F0.wireOp",EDGE,"E39.10.0.0"),sQuery(id+"F0.wireOp",EDGE,"E39.11.0.0"),sQuery(id+"F0.wireOp",EDGE,"E39.12.0.0"),sQuery(id+"F0.wireOp",EDGE,"E39.13.0.0"),sQuery(id+"F0.wireOp",EDGE,"E40.trimOffspring"),sQuery(id+"F0.wireOp",EDGE,"E41.trimOffspring"),sQuery(id+"F0.wireOp",EDGE,"E42.trimOffspring"),sQuery(id+"F0.wireOp",EDGE,"E43.trimOffspring"),sQuery(id+"F0.wireOp",EDGE,"E44.trimOffspring"),sQuery(id+"F0.wireOp",EDGE,"E45.trimOffspring"),sQuery(id+"F0.wireOp",EDGE,"E46.trimOffspring"),sQuery(id+"F0.wireOp",EDGE,"E47.trimOffspring"),sQuery(id+"F0.wireOp",EDGE,"E48.trimOffspring"),sQuery(id+"F0.wireOp",EDGE,"E49.trimOffspring"),sQuery(id+"F0.wireOp",EDGE,"E50.trimOffspring"),sQuery(id+"F0.wireOp",EDGE,"E51.trimOffspring"),sQuery(id+"F0.wireOp",EDGE,"E52.trimOffspring"),sQuery(id+"F0.wireOp",EDGE,"E53.trimOffspring"),sQuery(id+"F0.wireOp",EDGE,"E54.MirrorC"),sQuery(id+"F0.wireOp",EDGE,"E55"),sQuery(id+"F0.wireOp",EDGE,"E56.0.1.0"),sQuery(id+"F0.wireOp",EDGE,"E56.0.2.0"),sQuery(id+"F0.wireOp",EDGE,"E56.0.3.0"),sQuery(id+"F0.wireOp",EDGE,"E56.0.4.0"),sQuery(id+"F0.wireOp",EDGE,"E56.0.5.0"),sQuery(id+"F0.wireOp",EDGE,"E56.0.6.0"),sQuery(id+"F0.wireOp",EDGE,"E56.0.7.0"),sQuery(id+"F0.wireOp",EDGE,"E56.0.8.0"),sQuery(id+"F0.wireOp",EDGE,"E56.0.9.0"),sQuery(id+"F0.wireOp",EDGE,"E56.0.10.0"),sQuery(id+"F0.wireOp",EDGE,"E56.0.11.0"),sQuery(id+"F0.wireOp",EDGE,"E57.trimOffspring"),sQuery(id+"F0.wireOp",EDGE,"E58.trimOffspring"),sQuery(id+"F0.wireOp",EDGE,"E59.trimOffspring"),sQuery(id+"F0.wireOp",EDGE,"E60.trimOffspring"),sQuery(id+"F0.wireOp",EDGE,"E61.trimOffspring"),sQuery(id+"F0.wireOp",EDGE,"E62.trimOffspring"),sQuery(id+"F0.wireOp",EDGE,"E63.trimOffspring"),sQuery(id+"F0.wireOp",EDGE,"E64.trimOffspring"),sQuery(id+"F0.wireOp",EDGE,"E65.trimOffspring"),sQuery(id+"F0.wireOp",EDGE,"E66.trimOffspring"),sQuery(id+"F0.wireOp",EDGE,"E67.trimOffspring"),sQuery(id+"F0.wireOp",EDGE,"E68.bottom"),sQuery(id+"F0.wireOp",EDGE,"E68.left"),sQuery(id+"F0.wireOp",EDGE,"E68.right"),sQuery(id+"F0.wireOp",EDGE,"E69.0.1.0"),sQuery(id+"F0.wireOp",EDGE,"E69.0.1.1"),sQuery(id+"F0.wireOp",EDGE,"E69.0.1.2"),sQuery(id+"F0.wireOp",EDGE,"E69.0.1.3"),sQuery(id+"F0.wireOp",EDGE,"E69.0.2.0"),sQuery(id+"F0.wireOp",EDGE,"E69.0.2.1"),sQuery(id+"F0.wireOp",EDGE,"E69.0.2.2"),sQuery(id+"F0.wireOp",EDGE,"E69.0.2.3"),sQuery(id+"F0.wireOp",EDGE,"E69.0.3.0"),sQuery(id+"F0.wireOp",EDGE,"E69.0.3.1"),sQuery(id+"F0.wireOp",EDGE,"E69.0.3.2"),sQuery(id+"F0.wireOp",EDGE,"E69.0.3.3"),sQuery(id+"F0.wireOp",EDGE,"E69.0.4.0"),sQuery(id+"F0.wireOp",EDGE,"E69.0.4.1"),sQuery(id+"F0.wireOp",EDGE,"E69.0.4.2"),sQuery(id+"F0.wireOp",EDGE,"E69.0.4.3"),sQuery(id+"F0.wireOp",EDGE,"E69.0.5.0"),sQuery(id+"F0.wireOp",EDGE,"E69.0.5.1"),sQuery(id+"F0.wireOp",EDGE,"E69.0.5.2"),sQuery(id+"F0.wireOp",EDGE,"E69.0.5.3"),sQuery(id+"F0.wireOp",EDGE,"E70.trimOffspring")])]});
            var Q1;
            Q1=makeQuery(id+"F6.opExtrude","SWEPT_BODY",BODY,{"disambiguationData":[OSD([sQuery(id+"F0.wireOp",EDGE,"E0.left"),sQuery(id+"F2.wireOp",EDGE,"E71.left"),sQuery(id+"F2.wireOp",EDGE,"E111"),sQuery(id+"F5.wireOp",EDGE,"E115"),sQuery(id+"F5.wireOp",EDGE,"E116"),sQuery(id+"F5.wireOp",EDGE,"E117"),sQuery(id+"F5.wireOp",EDGE,"E118"),sQuery(id+"F5.wireOp",EDGE,"E119"),sQuery(id+"F5.wireOp",EDGE,"E120"),sQuery(id+"F5.wireOp",EDGE,"E121"),sQuery(id+"F5.wireOp",EDGE,"E122"),sQuery(id+"F5.wireOp",EDGE,"E124"),sQuery(id+"F5.wireOp",EDGE,"E125"),sQuery(id+"F5.wireOp",EDGE,"E126"),sQuery(id+"F5.wireOp",EDGE,"E127.0.1.0"),sQuery(id+"F5.wireOp",EDGE,"E127.0.1.1"),sQuery(id+"F5.wireOp",EDGE,"E127.0.1.2"),sQuery(id+"F5.wireOp",EDGE,"E127.0.2.0"),sQuery(id+"F5.wireOp",EDGE,"E127.0.2.1"),sQuery(id+"F5.wireOp",EDGE,"E127.0.2.2"),sQuery(id+"F5.wireOp",EDGE,"E127.0.3.0"),sQuery(id+"F5.wireOp",EDGE,"E127.0.3.1"),sQuery(id+"F5.wireOp",EDGE,"E127.0.3.2"),sQuery(id+"F5.wireOp",EDGE,"E128.trimOffspring"),sQuery(id+"F5.wireOp",EDGE,"E129.trimOffspring"),sQuery(id+"F5.wireOp",EDGE,"E130.trimOffspring"),sQuery(id+"F5.wireOp",EDGE,"E131.trimOffspring"),sQuery(id+"F5.wireOp",EDGE,"E132"),sQuery(id+"F5.wireOp",EDGE,"E133"),sQuery(id+"F5.wireOp",EDGE,"E134.1.0.0"),sQuery(id+"F5.wireOp",EDGE,"E134.2.0.0"),sQuery(id+"F5.wireOp",EDGE,"E134.3.0.0"),sQuery(id+"F5.wireOp",EDGE,"E134.4.0.0"),sQuery(id+"F5.wireOp",EDGE,"E135"),sQuery(id+"F5.wireOp",EDGE,"E136"),sQuery(id+"F5.wireOp",EDGE,"E137.trimOffspring"),sQuery(id+"F5.wireOp",EDGE,"E138.trimOffspring")])]});
            var Q2;
            Q2=makeQuery(id+"F7.opPattern","COPY",BODY,{"derivedFrom":makeQuery(id+"F6.opExtrude","SWEPT_BODY",BODY,{"disambiguationData":[OSD([sQuery(id+"F0.wireOp",EDGE,"E0.left"),sQuery(id+"F2.wireOp",EDGE,"E71.left"),sQuery(id+"F2.wireOp",EDGE,"E111"),sQuery(id+"F5.wireOp",EDGE,"E115"),sQuery(id+"F5.wireOp",EDGE,"E116"),sQuery(id+"F5.wireOp",EDGE,"E117"),sQuery(id+"F5.wireOp",EDGE,"E118"),sQuery(id+"F5.wireOp",EDGE,"E119"),sQuery(id+"F5.wireOp",EDGE,"E120"),sQuery(id+"F5.wireOp",EDGE,"E121"),sQuery(id+"F5.wireOp",EDGE,"E122"),sQuery(id+"F5.wireOp",EDGE,"E124"),sQuery(id+"F5.wireOp",EDGE,"E125"),sQuery(id+"F5.wireOp",EDGE,"E126"),sQuery(id+"F5.wireOp",EDGE,"E127.0.1.0"),sQuery(id+"F5.wireOp",EDGE,"E127.0.1.1"),sQuery(id+"F5.wireOp",EDGE,"E127.0.1.2"),sQuery(id+"F5.wireOp",EDGE,"E127.0.2.0"),sQuery(id+"F5.wireOp",EDGE,"E127.0.2.1"),sQuery(id+"F5.wireOp",EDGE,"E127.0.2.2"),sQuery(id+"F5.wireOp",EDGE,"E127.0.3.0"),sQuery(id+"F5.wireOp",EDGE,"E127.0.3.1"),sQuery(id+"F5.wireOp",EDGE,"E127.0.3.2"),sQuery(id+"F5.wireOp",EDGE,"E128.trimOffspring"),sQuery(id+"F5.wireOp",EDGE,"E129.trimOffspring"),sQuery(id+"F5.wireOp",EDGE,"E130.trimOffspring"),sQuery(id+"F5.wireOp",EDGE,"E131.trimOffspring"),sQuery(id+"F5.wireOp",EDGE,"E132"),sQuery(id+"F5.wireOp",EDGE,"E133"),sQuery(id+"F5.wireOp",EDGE,"E134.1.0.0"),sQuery(id+"F5.wireOp",EDGE,"E134.2.0.0"),sQuery(id+"F5.wireOp",EDGE,"E134.3.0.0"),sQuery(id+"F5.wireOp",EDGE,"E134.4.0.0"),sQuery(id+"F5.wireOp",EDGE,"E135"),sQuery(id+"F5.wireOp",EDGE,"E136"),sQuery(id+"F5.wireOp",EDGE,"E137.trimOffspring"),sQuery(id+"F5.wireOp",EDGE,"E138.trimOffspring")])]}),"instanceName":"1"});
            var Q3;
            Q3=makeQuery(id+"F9.opPattern","COPY",BODY,{"derivedFrom":makeQuery(id+"F6.opExtrude","SWEPT_BODY",BODY,{"disambiguationData":[OSD([sQuery(id+"F0.wireOp",EDGE,"E0.left"),sQuery(id+"F2.wireOp",EDGE,"E71.left"),sQuery(id+"F2.wireOp",EDGE,"E111"),sQuery(id+"F5.wireOp",EDGE,"E115"),sQuery(id+"F5.wireOp",EDGE,"E116"),sQuery(id+"F5.wireOp",EDGE,"E117"),sQuery(id+"F5.wireOp",EDGE,"E118"),sQuery(id+"F5.wireOp",EDGE,"E119"),sQuery(id+"F5.wireOp",EDGE,"E120"),sQuery(id+"F5.wireOp",EDGE,"E121"),sQuery(id+"F5.wireOp",EDGE,"E122"),sQuery(id+"F5.wireOp",EDGE,"E124"),sQuery(id+"F5.wireOp",EDGE,"E125"),sQuery(id+"F5.wireOp",EDGE,"E126"),sQuery(id+"F5.wireOp",EDGE,"E127.0.1.0"),sQuery(id+"F5.wireOp",EDGE,"E127.0.1.1"),sQuery(id+"F5.wireOp",EDGE,"E127.0.1.2"),sQuery(id+"F5.wireOp",EDGE,"E127.0.2.0"),sQuery(id+"F5.wireOp",EDGE,"E127.0.2.1"),sQuery(id+"F5.wireOp",EDGE,"E127.0.2.2"),sQuery(id+"F5.wireOp",EDGE,"E127.0.3.0"),sQuery(id+"F5.wireOp",EDGE,"E127.0.3.1"),sQuery(id+"F5.wireOp",EDGE,"E127.0.3.2"),sQuery(id+"F5.wireOp",EDGE,"E128.trimOffspring"),sQuery(id+"F5.wireOp",EDGE,"E129.trimOffspring"),sQuery(id+"F5.wireOp",EDGE,"E130.trimOffspring"),sQuery(id+"F5.wireOp",EDGE,"E131.trimOffspring"),sQuery(id+"F5.wireOp",EDGE,"E132"),sQuery(id+"F5.wireOp",EDGE,"E133"),sQuery(id+"F5.wireOp",EDGE,"E134.1.0.0"),sQuery(id+"F5.wireOp",EDGE,"E134.2.0.0"),sQuery(id+"F5.wireOp",EDGE,"E134.3.0.0"),sQuery(id+"F5.wireOp",EDGE,"E134.4.0.0"),sQuery(id+"F5.wireOp",EDGE,"E135"),sQuery(id+"F5.wireOp",EDGE,"E136"),sQuery(id+"F5.wireOp",EDGE,"E137.trimOffspring"),sQuery(id+"F5.wireOp",EDGE,"E138.trimOffspring")])]}),"instanceName":"1"});
            var Q4;
            Q4=makeQuery(id+"F12.opExtrude","SWEPT_BODY",BODY,{"disambiguationData":[OSD([sQuery(id+"F11.wireOp",EDGE,"E139.bottom"),sQuery(id+"F11.wireOp",EDGE,"E139.top"),sQuery(id+"F11.wireOp",EDGE,"E139.left"),sQuery(id+"F11.wireOp",EDGE,"E139.right"),sQuery(id+"F11.wireOp",EDGE,"E140"),sQuery(id+"F11.wireOp",EDGE,"E141"),sQuery(id+"F11.wireOp",EDGE,"E142.1.0.0"),sQuery(id+"F11.wireOp",EDGE,"E142.2.0.0"),sQuery(id+"F11.wireOp",EDGE,"E142.3.0.0"),sQuery(id+"F11.wireOp",EDGE,"E142.4.0.0"),sQuery(id+"F11.wireOp",EDGE,"E142.5.0.0"),sQuery(id+"F11.wireOp",EDGE,"E142.6.0.0"),sQuery(id+"F11.wireOp",EDGE,"E142.7.0.0"),sQuery(id+"F11.wireOp",EDGE,"E142.8.0.0"),sQuery(id+"F11.wireOp",EDGE,"E142.9.0.0"),sQuery(id+"F11.wireOp",EDGE,"E142.10.0.0"),sQuery(id+"F11.wireOp",EDGE,"E142.11.0.0"),sQuery(id+"F11.wireOp",EDGE,"E142.12.0.0"),sQuery(id+"F11.wireOp",EDGE,"E142.13.0.0"),sQuery(id+"F11.wireOp",EDGE,"E143.trimOffspring"),sQuery(id+"F11.wireOp",EDGE,"E144.trimOffspring"),sQuery(id+"F11.wireOp",EDGE,"E145.trimOffspring"),sQuery(id+"F11.wireOp",EDGE,"E146.trimOffspring"),sQuery(id+"F11.wireOp",EDGE,"E147.trimOffspring"),sQuery(id+"F11.wireOp",EDGE,"E148.trimOffspring"),sQuery(id+"F11.wireOp",EDGE,"E149.trimOffspring"),sQuery(id+"F11.wireOp",EDGE,"E150.trimOffspring"),sQuery(id+"F11.wireOp",EDGE,"E151.trimOffspring"),sQuery(id+"F11.wireOp",EDGE,"E152.trimOffspring"),sQuery(id+"F11.wireOp",EDGE,"E153.trimOffspring"),sQuery(id+"F11.wireOp",EDGE,"E154.trimOffspring"),sQuery(id+"F11.wireOp",EDGE,"E155.trimOffspring")])]});
            booleanBodies(context, id + "F13", {"operationType" : BooleanOperationType.SUBTRACTION, "tools" : qUnion([Q0, Q1, Q2, Q3]), "targets" : qUnion([Q4]), "keepTools" : true});
        }
        {
            var Q0;
            Q0=makeQuery(id+"F7.opPattern","COPY",FACE,{"derivedFrom":makeQuery(id+"F6.opExtrude","SWEPT_FACE",FACE,{"disambiguationData":[OSD([sQuery(id+"F5.wireOp",EDGE,"E131.trimOffspring")])]}),"instanceName":"1"});
            var sketch = newSketch(context, id + "F14", { "sketchPlane" : qUnion([Q0])});
            skLineSegment(sketch, "E156.bottom", {"start": v(-150, -150) * mm, "end": v(150, -150) * mm});
            skLineSegment(sketch, "E156.top", {"start": v(-150, 26) * mm, "end": v(150, 26) * mm});
            skLineSegment(sketch, "E156.left", {"start": v(-150, -150) * mm, "end": v(-150, 26) * mm});
            skLineSegment(sketch, "E156.right", {"start": v(150, -150) * mm, "end": v(150, 26) * mm});
            skSolve(sketch);
        }
        {
            var Q0;
            Q0=makeQuery(id+"F14.imprint","IMPRINT",FACE,{"disambiguationData":[TD([[makeQuery(id+"F14.imprint","IMPRINT",EDGE,{"derivedFrom":sQuery(id+"F14.wireOp",EDGE,"E156.bottom")}),1.0]])]});
            extrude(context, id + "F15", {"entities" : qUnion([Q0]), "oppositeDirection" : true, "depth" : 4 * mm});
        }
        {
            var Q0;
            Q0=makeQuery(id+"F12.opExtrude","SWEPT_BODY",BODY,{"disambiguationData":[OSD([sQuery(id+"F11.wireOp",EDGE,"E139.bottom"),sQuery(id+"F11.wireOp",EDGE,"E139.top"),sQuery(id+"F11.wireOp",EDGE,"E139.left"),sQuery(id+"F11.wireOp",EDGE,"E139.right"),sQuery(id+"F11.wireOp",EDGE,"E140"),sQuery(id+"F11.wireOp",EDGE,"E141"),sQuery(id+"F11.wireOp",EDGE,"E142.1.0.0"),sQuery(id+"F11.wireOp",EDGE,"E142.2.0.0"),sQuery(id+"F11.wireOp",EDGE,"E142.3.0.0"),sQuery(id+"F11.wireOp",EDGE,"E142.4.0.0"),sQuery(id+"F11.wireOp",EDGE,"E142.5.0.0"),sQuery(id+"F11.wireOp",EDGE,"E142.6.0.0"),sQuery(id+"F11.wireOp",EDGE,"E142.7.0.0"),sQuery(id+"F11.wireOp",EDGE,"E142.8.0.0"),sQuery(id+"F11.wireOp",EDGE,"E142.9.0.0"),sQuery(id+"F11.wireOp",EDGE,"E142.10.0.0"),sQuery(id+"F11.wireOp",EDGE,"E142.11.0.0"),sQuery(id+"F11.wireOp",EDGE,"E142.12.0.0"),sQuery(id+"F11.wireOp",EDGE,"E142.13.0.0"),sQuery(id+"F11.wireOp",EDGE,"E143.trimOffspring"),sQuery(id+"F11.wireOp",EDGE,"E144.trimOffspring"),sQuery(id+"F11.wireOp",EDGE,"E145.trimOffspring"),sQuery(id+"F11.wireOp",EDGE,"E146.trimOffspring"),sQuery(id+"F11.wireOp",EDGE,"E147.trimOffspring"),sQuery(id+"F11.wireOp",EDGE,"E148.trimOffspring"),sQuery(id+"F11.wireOp",EDGE,"E149.trimOffspring"),sQuery(id+"F11.wireOp",EDGE,"E150.trimOffspring"),sQuery(id+"F11.wireOp",EDGE,"E151.trimOffspring"),sQuery(id+"F11.wireOp",EDGE,"E152.trimOffspring"),sQuery(id+"F11.wireOp",EDGE,"E153.trimOffspring"),sQuery(id+"F11.wireOp",EDGE,"E154.trimOffspring"),sQuery(id+"F11.wireOp",EDGE,"E155.trimOffspring")])]});
            var Q1;
            Q1=makeQuery(id+"F9.opPattern","COPY",BODY,{"derivedFrom":makeQuery(id+"F6.opExtrude","SWEPT_BODY",BODY,{"disambiguationData":[OSD([sQuery(id+"F0.wireOp",EDGE,"E0.left"),sQuery(id+"F2.wireOp",EDGE,"E71.left"),sQuery(id+"F2.wireOp",EDGE,"E111"),sQuery(id+"F5.wireOp",EDGE,"E115"),sQuery(id+"F5.wireOp",EDGE,"E116"),sQuery(id+"F5.wireOp",EDGE,"E117"),sQuery(id+"F5.wireOp",EDGE,"E118"),sQuery(id+"F5.wireOp",EDGE,"E119"),sQuery(id+"F5.wireOp",EDGE,"E120"),sQuery(id+"F5.wireOp",EDGE,"E121"),sQuery(id+"F5.wireOp",EDGE,"E122"),sQuery(id+"F5.wireOp",EDGE,"E124"),sQuery(id+"F5.wireOp",EDGE,"E125"),sQuery(id+"F5.wireOp",EDGE,"E126"),sQuery(id+"F5.wireOp",EDGE,"E127.0.1.0"),sQuery(id+"F5.wireOp",EDGE,"E127.0.1.1"),sQuery(id+"F5.wireOp",EDGE,"E127.0.1.2"),sQuery(id+"F5.wireOp",EDGE,"E127.0.2.0"),sQuery(id+"F5.wireOp",EDGE,"E127.0.2.1"),sQuery(id+"F5.wireOp",EDGE,"E127.0.2.2"),sQuery(id+"F5.wireOp",EDGE,"E127.0.3.0"),sQuery(id+"F5.wireOp",EDGE,"E127.0.3.1"),sQuery(id+"F5.wireOp",EDGE,"E127.0.3.2"),sQuery(id+"F5.wireOp",EDGE,"E128.trimOffspring"),sQuery(id+"F5.wireOp",EDGE,"E129.trimOffspring"),sQuery(id+"F5.wireOp",EDGE,"E130.trimOffspring"),sQuery(id+"F5.wireOp",EDGE,"E131.trimOffspring"),sQuery(id+"F5.wireOp",EDGE,"E132"),sQuery(id+"F5.wireOp",EDGE,"E133"),sQuery(id+"F5.wireOp",EDGE,"E134.1.0.0"),sQuery(id+"F5.wireOp",EDGE,"E134.2.0.0"),sQuery(id+"F5.wireOp",EDGE,"E134.3.0.0"),sQuery(id+"F5.wireOp",EDGE,"E134.4.0.0"),sQuery(id+"F5.wireOp",EDGE,"E135"),sQuery(id+"F5.wireOp",EDGE,"E136"),sQuery(id+"F5.wireOp",EDGE,"E137.trimOffspring"),sQuery(id+"F5.wireOp",EDGE,"E138.trimOffspring")])]}),"instanceName":"1"});
            var Q2;
            Q2=makeQuery(id+"F7.opPattern","COPY",BODY,{"derivedFrom":makeQuery(id+"F6.opExtrude","SWEPT_BODY",BODY,{"disambiguationData":[OSD([sQuery(id+"F0.wireOp",EDGE,"E0.left"),sQuery(id+"F2.wireOp",EDGE,"E71.left"),sQuery(id+"F2.wireOp",EDGE,"E111"),sQuery(id+"F5.wireOp",EDGE,"E115"),sQuery(id+"F5.wireOp",EDGE,"E116"),sQuery(id+"F5.wireOp",EDGE,"E117"),sQuery(id+"F5.wireOp",EDGE,"E118"),sQuery(id+"F5.wireOp",EDGE,"E119"),sQuery(id+"F5.wireOp",EDGE,"E120"),sQuery(id+"F5.wireOp",EDGE,"E121"),sQuery(id+"F5.wireOp",EDGE,"E122"),sQuery(id+"F5.wireOp",EDGE,"E124"),sQuery(id+"F5.wireOp",EDGE,"E125"),sQuery(id+"F5.wireOp",EDGE,"E126"),sQuery(id+"F5.wireOp",EDGE,"E127.0.1.0"),sQuery(id+"F5.wireOp",EDGE,"E127.0.1.1"),sQuery(id+"F5.wireOp",EDGE,"E127.0.1.2"),sQuery(id+"F5.wireOp",EDGE,"E127.0.2.0"),sQuery(id+"F5.wireOp",EDGE,"E127.0.2.1"),sQuery(id+"F5.wireOp",EDGE,"E127.0.2.2"),sQuery(id+"F5.wireOp",EDGE,"E127.0.3.0"),sQuery(id+"F5.wireOp",EDGE,"E127.0.3.1"),sQuery(id+"F5.wireOp",EDGE,"E127.0.3.2"),sQuery(id+"F5.wireOp",EDGE,"E128.trimOffspring"),sQuery(id+"F5.wireOp",EDGE,"E129.trimOffspring"),sQuery(id+"F5.wireOp",EDGE,"E130.trimOffspring"),sQuery(id+"F5.wireOp",EDGE,"E131.trimOffspring"),sQuery(id+"F5.wireOp",EDGE,"E132"),sQuery(id+"F5.wireOp",EDGE,"E133"),sQuery(id+"F5.wireOp",EDGE,"E134.1.0.0"),sQuery(id+"F5.wireOp",EDGE,"E134.2.0.0"),sQuery(id+"F5.wireOp",EDGE,"E134.3.0.0"),sQuery(id+"F5.wireOp",EDGE,"E134.4.0.0"),sQuery(id+"F5.wireOp",EDGE,"E135"),sQuery(id+"F5.wireOp",EDGE,"E136"),sQuery(id+"F5.wireOp",EDGE,"E137.trimOffspring"),sQuery(id+"F5.wireOp",EDGE,"E138.trimOffspring")])]}),"instanceName":"1"});
            var Q3;
            Q3=makeQuery(id+"F6.opExtrude","SWEPT_BODY",BODY,{"disambiguationData":[OSD([sQuery(id+"F0.wireOp",EDGE,"E0.left"),sQuery(id+"F2.wireOp",EDGE,"E71.left"),sQuery(id+"F2.wireOp",EDGE,"E111"),sQuery(id+"F5.wireOp",EDGE,"E115"),sQuery(id+"F5.wireOp",EDGE,"E116"),sQuery(id+"F5.wireOp",EDGE,"E117"),sQuery(id+"F5.wireOp",EDGE,"E118"),sQuery(id+"F5.wireOp",EDGE,"E119"),sQuery(id+"F5.wireOp",EDGE,"E120"),sQuery(id+"F5.wireOp",EDGE,"E121"),sQuery(id+"F5.wireOp",EDGE,"E122"),sQuery(id+"F5.wireOp",EDGE,"E124"),sQuery(id+"F5.wireOp",EDGE,"E125"),sQuery(id+"F5.wireOp",EDGE,"E126"),sQuery(id+"F5.wireOp",EDGE,"E127.0.1.0"),sQuery(id+"F5.wireOp",EDGE,"E127.0.1.1"),sQuery(id+"F5.wireOp",EDGE,"E127.0.1.2"),sQuery(id+"F5.wireOp",EDGE,"E127.0.2.0"),sQuery(id+"F5.wireOp",EDGE,"E127.0.2.1"),sQuery(id+"F5.wireOp",EDGE,"E127.0.2.2"),sQuery(id+"F5.wireOp",EDGE,"E127.0.3.0"),sQuery(id+"F5.wireOp",EDGE,"E127.0.3.1"),sQuery(id+"F5.wireOp",EDGE,"E127.0.3.2"),sQuery(id+"F5.wireOp",EDGE,"E128.trimOffspring"),sQuery(id+"F5.wireOp",EDGE,"E129.trimOffspring"),sQuery(id+"F5.wireOp",EDGE,"E130.trimOffspring"),sQuery(id+"F5.wireOp",EDGE,"E131.trimOffspring"),sQuery(id+"F5.wireOp",EDGE,"E132"),sQuery(id+"F5.wireOp",EDGE,"E133"),sQuery(id+"F5.wireOp",EDGE,"E134.1.0.0"),sQuery(id+"F5.wireOp",EDGE,"E134.2.0.0"),sQuery(id+"F5.wireOp",EDGE,"E134.3.0.0"),sQuery(id+"F5.wireOp",EDGE,"E134.4.0.0"),sQuery(id+"F5.wireOp",EDGE,"E135"),sQuery(id+"F5.wireOp",EDGE,"E136"),sQuery(id+"F5.wireOp",EDGE,"E137.trimOffspring"),sQuery(id+"F5.wireOp",EDGE,"E138.trimOffspring")])]});
            var Q4;
            Q4=makeQuery(id+"F15.opExtrude","SWEPT_BODY",BODY,{"disambiguationData":[OSD([sQuery(id+"F5.wireOp",EDGE,"E124"),sQuery(id+"F5.wireOp",EDGE,"E131.trimOffspring"),sQuery(id+"F14.wireOp",EDGE,"E156.bottom"),sQuery(id+"F14.wireOp",EDGE,"E156.top"),sQuery(id+"F14.wireOp",EDGE,"E156.left"),sQuery(id+"F14.wireOp",EDGE,"E156.right")])]});
            booleanBodies(context, id + "F16", {"operationType" : BooleanOperationType.SUBTRACTION, "tools" : qUnion([Q0, Q1, Q2, Q3]), "targets" : qUnion([Q4]), "keepTools" : true});
        }
    });
